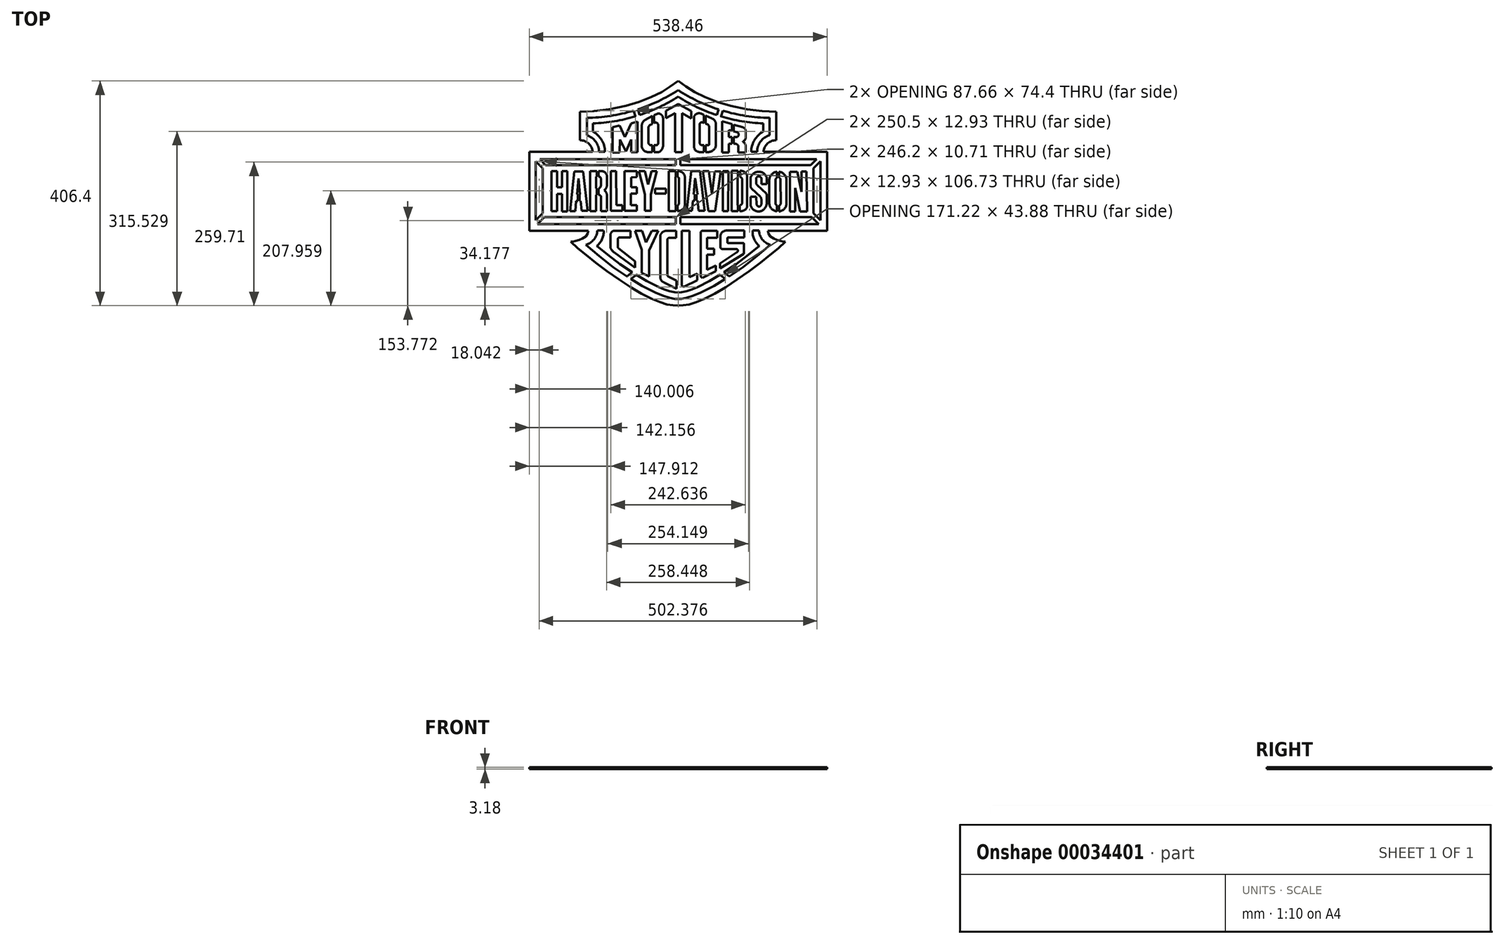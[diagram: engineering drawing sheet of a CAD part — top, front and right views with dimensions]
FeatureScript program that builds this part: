
annotation { "Feature Type Name" : "Feature", "Feature Type Description" : "" }
export const myFeature = defineFeature(function(context is Context, id is Id, definition is map)
    precondition{}
    {
        {
            var Q0;
            Q0=qCreatedBy(makeId("Top.planeOp"),FACE);
            var sketch = newSketch(context, id + "F0", { "sketchPlane" : qUnion([Q0])});
            skLineSegment(sketch, "E0", {"start": v(244.72, 45.2) * mm, "end": v(244.72, -35.68) * mm});
            skLineSegment(sketch, "E1", {"start": v(244.72, 45.2) * mm, "end": v(257.65, 58.13) * mm});
            skLineSegment(sketch, "E2", {"start": v(257.65, -48.6) * mm, "end": v(257.65, 58.13) * mm});
            skLineSegment(sketch, "E3", {"start": v(257.65, -48.6) * mm, "end": v(244.72, -35.68) * mm});
            skLineSegment(sketch, "E4", {"start": v(-134.72, -67.36) * mm, "end": v(-146, -67.36) * mm});
            skArc(sketch, "E5", {"start": v(-134.72, -67.36) * mm, "mid": v(-137.31, -82.59) * mm, "end": v(-146.79, -94.79) * mm});
            skLineSegment(sketch, "E6", {"start": v(-127.25, -111.1) * mm, "end": v(-146.79, -94.79) * mm});
            skLineSegment(sketch, "E7", {"start": v(-104.97, -127.73) * mm, "end": v(-127.25, -111.1) * mm});
            skLineSegment(sketch, "E8", {"start": v(-79.29, -145.04) * mm, "end": v(-104.97, -127.73) * mm});
            skLineSegment(sketch, "E9", {"start": v(-56.85, -158.5) * mm, "end": v(-79.29, -145.04) * mm});
            skLineSegment(sketch, "E10", {"start": v(-35.61, -169.16) * mm, "end": v(-56.85, -158.5) * mm});
            skLineSegment(sketch, "E11", {"start": v(-24.96, -173.53) * mm, "end": v(-35.61, -169.16) * mm});
            skLineSegment(sketch, "E12", {"start": v(-15.65, -176.7) * mm, "end": v(-24.96, -173.53) * mm});
            skLineSegment(sketch, "E13", {"start": v(-6.27, -178.92) * mm, "end": v(-15.65, -176.7) * mm});
            skLineSegment(sketch, "E14", {"start": v(0, -179.18) * mm, "end": v(-6.27, -178.92) * mm});
            skLineSegment(sketch, "E15", {"start": v(0, -179.18) * mm, "end": v(6.27, -178.92) * mm});
            skLineSegment(sketch, "E16", {"start": v(6.27, -178.92) * mm, "end": v(15.65, -176.7) * mm});
            skLineSegment(sketch, "E17", {"start": v(15.65, -176.7) * mm, "end": v(24.96, -173.53) * mm});
            skLineSegment(sketch, "E18", {"start": v(24.96, -173.53) * mm, "end": v(35.61, -169.16) * mm});
            skLineSegment(sketch, "E19", {"start": v(35.61, -169.16) * mm, "end": v(56.85, -158.5) * mm});
            skLineSegment(sketch, "E20", {"start": v(56.85, -158.5) * mm, "end": v(79.29, -145.04) * mm});
            skLineSegment(sketch, "E21", {"start": v(79.29, -145.04) * mm, "end": v(104.97, -127.73) * mm});
            skLineSegment(sketch, "E22", {"start": v(104.97, -127.73) * mm, "end": v(127.25, -111.1) * mm});
            skLineSegment(sketch, "E23", {"start": v(127.25, -111.1) * mm, "end": v(146.79, -94.79) * mm});
            skArc(sketch, "E24", {"start": v(134.72, -67.36) * mm, "mid": v(137.31, -82.59) * mm, "end": v(146.79, -94.79) * mm});
            skLineSegment(sketch, "E25", {"start": v(134.72, -67.36) * mm, "end": v(146, -67.36) * mm});
            skArc(sketch, "E26", {"start": v(146, -67.36) * mm, "mid": v(152.34, -83.41) * mm, "end": v(166.67, -93.03) * mm});
            skLineSegment(sketch, "E27", {"start": v(142.64, -113.33) * mm, "end": v(166.67, -93.03) * mm});
            skLineSegment(sketch, "E28", {"start": v(117.12, -133.46) * mm, "end": v(142.64, -113.33) * mm});
            skLineSegment(sketch, "E29", {"start": v(89.28, -152.75) * mm, "end": v(117.12, -133.46) * mm});
            skLineSegment(sketch, "E30", {"start": v(64.94, -167.27) * mm, "end": v(89.28, -152.75) * mm});
            skLineSegment(sketch, "E31", {"start": v(40.94, -179.2) * mm, "end": v(64.94, -167.27) * mm});
            skLineSegment(sketch, "E32", {"start": v(26.9, -184.96) * mm, "end": v(40.94, -179.2) * mm});
            skLineSegment(sketch, "E33", {"start": v(14.99, -188.9) * mm, "end": v(26.9, -184.96) * mm});
            skLineSegment(sketch, "E34", {"start": v(6.15, -190.75) * mm, "end": v(14.99, -188.9) * mm});
            skLineSegment(sketch, "E35", {"start": v(0, -190.96) * mm, "end": v(6.15, -190.75) * mm});
            skLineSegment(sketch, "E36", {"start": v(0, -190.96) * mm, "end": v(-6.15, -190.75) * mm});
            skLineSegment(sketch, "E37", {"start": v(-6.15, -190.75) * mm, "end": v(-14.99, -188.9) * mm});
            skLineSegment(sketch, "E38", {"start": v(-14.99, -188.9) * mm, "end": v(-26.9, -184.96) * mm});
            skLineSegment(sketch, "E39", {"start": v(-26.9, -184.96) * mm, "end": v(-40.94, -179.2) * mm});
            skLineSegment(sketch, "E40", {"start": v(-40.94, -179.2) * mm, "end": v(-64.94, -167.27) * mm});
            skLineSegment(sketch, "E41", {"start": v(-64.94, -167.27) * mm, "end": v(-89.28, -152.75) * mm});
            skLineSegment(sketch, "E42", {"start": v(-89.28, -152.75) * mm, "end": v(-117.12, -133.46) * mm});
            skLineSegment(sketch, "E43", {"start": v(-117.12, -133.46) * mm, "end": v(-142.64, -113.33) * mm});
            skLineSegment(sketch, "E44", {"start": v(-142.64, -113.33) * mm, "end": v(-166.67, -93.03) * mm});
            skArc(sketch, "E45", {"start": v(-146, -67.36) * mm, "mid": v(-152.34, -83.41) * mm, "end": v(-166.67, -93.03) * mm});
            skArc(sketch, "E46", {"start": v(0, 186.68) * mm, "mid": v(-79.05, 150) * mm, "end": v(-165.15, 136.55) * mm});
            skArc(sketch, "E47", {"start": v(0, 186.68) * mm, "mid": v(79.05, 150) * mm, "end": v(165.15, 136.55) * mm});
            skLineSegment(sketch, "E48", {"start": v(165.15, 104.94) * mm, "end": v(165.15, 136.55) * mm});
            skArc(sketch, "E49", {"start": v(165.15, 104.94) * mm, "mid": v(149.13, 93.71) * mm, "end": v(143.02, 75.13) * mm});
            skLineSegment(sketch, "E50", {"start": v(132.18, 75.13) * mm, "end": v(143.02, 75.13) * mm});
            skArc(sketch, "E51", {"start": v(153.86, 111.71) * mm, "mid": v(138.12, 96.32) * mm, "end": v(132.18, 75.13) * mm});
            skLineSegment(sketch, "E52", {"start": v(153.86, 111.71) * mm, "end": v(153.86, 126.62) * mm});
            skArc(sketch, "E53", {"start": v(0, 174.94) * mm, "mid": v(73.69, 140.46) * mm, "end": v(153.86, 126.62) * mm});
            skArc(sketch, "E54", {"start": v(0, 174.94) * mm, "mid": v(-73.69, 140.46) * mm, "end": v(-153.86, 126.62) * mm});
            skLineSegment(sketch, "E55", {"start": v(-153.86, 111.71) * mm, "end": v(-153.86, 126.62) * mm});
            skArc(sketch, "E56", {"start": v(-153.86, 111.71) * mm, "mid": v(-138.12, 96.32) * mm, "end": v(-132.18, 75.13) * mm});
            skLineSegment(sketch, "E57", {"start": v(-132.18, 75.13) * mm, "end": v(-143.02, 75.13) * mm});
            skArc(sketch, "E58", {"start": v(-165.15, 104.94) * mm, "mid": v(-149.13, 93.71) * mm, "end": v(-143.02, 75.13) * mm});
            skLineSegment(sketch, "E59", {"start": v(-165.15, 104.94) * mm, "end": v(-165.15, 136.55) * mm});
            skLineSegment(sketch, "E60", {"start": v(250.17, 61.87) * mm, "end": v(-250.17, 61.87) * mm});
            skLineSegment(sketch, "E61", {"start": v(239.46, 51.15) * mm, "end": v(250.17, 61.87) * mm});
            skLineSegment(sketch, "E62", {"start": v(239.46, 51.15) * mm, "end": v(-239.46, 51.15) * mm});
            skLineSegment(sketch, "E63", {"start": v(-239.46, 51.15) * mm, "end": v(-250.17, 61.87) * mm});
            skLineSegment(sketch, "E64", {"start": v(-244.72, 45.2) * mm, "end": v(-257.65, 58.13) * mm});
            skLineSegment(sketch, "E65", {"start": v(-244.72, 45.2) * mm, "end": v(-244.72, -35.68) * mm});
            skLineSegment(sketch, "E66", {"start": v(-257.65, -48.6) * mm, "end": v(-244.72, -35.68) * mm});
            skLineSegment(sketch, "E67", {"start": v(-257.65, -48.6) * mm, "end": v(-257.65, 58.13) * mm});
            skLineSegment(sketch, "E68", {"start": v(-163.33, -31.77) * mm, "end": v(-172.1, 39.88) * mm});
            skLineSegment(sketch, "E69", {"start": v(-174.33, -31.77) * mm, "end": v(-163.33, -31.77) * mm});
            skLineSegment(sketch, "E70", {"start": v(-176.14, -13.56) * mm, "end": v(-174.33, -31.77) * mm});
            skLineSegment(sketch, "E71", {"start": v(-178.4, -13.56) * mm, "end": v(-176.14, -13.56) * mm});
            skLineSegment(sketch, "E72", {"start": v(-178.4, -1.4) * mm, "end": v(-178.4, -13.56) * mm});
            skLineSegment(sketch, "E73", {"start": v(-178.4, -1.4) * mm, "end": v(-177.53, -1.4) * mm});
            skLineSegment(sketch, "E74", {"start": v(-177.53, -1.4) * mm, "end": v(-180.35, 27.13) * mm});
            skLineSegment(sketch, "E75", {"start": v(-180.35, 27.13) * mm, "end": v(-182.47, -1.4) * mm});
            skLineSegment(sketch, "E76", {"start": v(-182.47, -1.4) * mm, "end": v(-181.58, -1.4) * mm});
            skLineSegment(sketch, "E77", {"start": v(-181.58, -1.4) * mm, "end": v(-181.58, -13.56) * mm});
            skLineSegment(sketch, "E78", {"start": v(-184.18, -13.56) * mm, "end": v(-181.58, -13.56) * mm});
            skLineSegment(sketch, "E79", {"start": v(-186.06, -31.82) * mm, "end": v(-184.18, -13.56) * mm});
            skLineSegment(sketch, "E80", {"start": v(-195.2, -31.82) * mm, "end": v(-186.06, -31.82) * mm});
            skLineSegment(sketch, "E81", {"start": v(-187.4, 39.88) * mm, "end": v(-195.2, -31.82) * mm});
            skLineSegment(sketch, "E82", {"start": v(-172.1, 39.88) * mm, "end": v(-187.4, 39.88) * mm});
            skLineSegment(sketch, "E83", {"start": v(-219.07, 40.27) * mm, "end": v(-228.97, 40.27) * mm});
            skLineSegment(sketch, "E84", {"start": v(-219.07, 11.13) * mm, "end": v(-219.07, 40.27) * mm});
            skLineSegment(sketch, "E85", {"start": v(-210.2, 11.13) * mm, "end": v(-219.07, 11.13) * mm});
            skLineSegment(sketch, "E86", {"start": v(-210.2, 40.02) * mm, "end": v(-210.2, 11.13) * mm});
            skLineSegment(sketch, "E87", {"start": v(-200.08, 40.02) * mm, "end": v(-210.2, 40.02) * mm});
            skLineSegment(sketch, "E88", {"start": v(-200.08, -32.47) * mm, "end": v(-200.08, 40.02) * mm});
            skLineSegment(sketch, "E89", {"start": v(-209.7, -32.47) * mm, "end": v(-200.08, -32.47) * mm});
            skLineSegment(sketch, "E90", {"start": v(-209.7, -1.04) * mm, "end": v(-209.7, -32.47) * mm});
            skLineSegment(sketch, "E91", {"start": v(-219.09, -1.04) * mm, "end": v(-209.7, -1.04) * mm});
            skLineSegment(sketch, "E92", {"start": v(-219.09, -32.22) * mm, "end": v(-219.09, -1.04) * mm});
            skLineSegment(sketch, "E93", {"start": v(-228.97, -32.22) * mm, "end": v(-219.09, -32.22) * mm});
            skLineSegment(sketch, "E94", {"start": v(-228.97, 40.27) * mm, "end": v(-228.97, -32.22) * mm});
            skArc(sketch, "E95", {"start": v(-59.31, 132.93) * mm, "mid": v(-63.89, 128.57) * mm, "end": v(-65.63, 122.5) * mm});
            skLineSegment(sketch, "E96", {"start": v(-46.78, 139.7) * mm, "end": v(-59.31, 132.93) * mm});
            skLineSegment(sketch, "E97", {"start": v(-46.78, 125.67) * mm, "end": v(-46.78, 139.7) * mm});
            skLineSegment(sketch, "E98", {"start": v(-50.02, 124.14) * mm, "end": v(-46.78, 125.67) * mm});
            skArc(sketch, "E99", {"start": v(-50.02, 124.14) * mm, "mid": v(-52.73, 121.7) * mm, "end": v(-53.61, 118.16) * mm});
            skLineSegment(sketch, "E100", {"start": v(-53.61, 91.84) * mm, "end": v(-53.61, 118.16) * mm});
            skArc(sketch, "E101", {"start": v(-53.61, 91.84) * mm, "mid": v(-52.12, 88.37) * mm, "end": v(-48.59, 87.06) * mm});
            skLineSegment(sketch, "E102", {"start": v(-46.78, 87.06) * mm, "end": v(-48.59, 87.06) * mm});
            skLineSegment(sketch, "E103", {"start": v(-46.78, 74.46) * mm, "end": v(-46.78, 87.06) * mm});
            skLineSegment(sketch, "E104", {"start": v(-46.78, 74.46) * mm, "end": v(-53.69, 74.46) * mm});
            skArc(sketch, "E105", {"start": v(-65.63, 84.09) * mm, "mid": v(-61.35, 77.17) * mm, "end": v(-53.69, 74.46) * mm});
            skLineSegment(sketch, "E106", {"start": v(-65.63, 122.5) * mm, "end": v(-65.63, 84.09) * mm});
            skLineSegment(sketch, "E107", {"start": v(23.7, 148.6) * mm, "end": v(0.36, 161.32) * mm});
            skLineSegment(sketch, "E108", {"start": v(23.7, 135.49) * mm, "end": v(23.7, 148.6) * mm});
            skLineSegment(sketch, "E109", {"start": v(7.5, 145.04) * mm, "end": v(23.7, 135.49) * mm});
            skLineSegment(sketch, "E110", {"start": v(7.5, 74.74) * mm, "end": v(7.5, 145.04) * mm});
            skLineSegment(sketch, "E111", {"start": v(-5.74, 74.74) * mm, "end": v(7.5, 74.74) * mm});
            skLineSegment(sketch, "E112", {"start": v(-5.74, 145.04) * mm, "end": v(-5.74, 74.74) * mm});
            skLineSegment(sketch, "E113", {"start": v(-22.1, 136.3) * mm, "end": v(-5.74, 145.04) * mm});
            skLineSegment(sketch, "E114", {"start": v(-22.1, 149.33) * mm, "end": v(-22.1, 136.3) * mm});
            skLineSegment(sketch, "E115", {"start": v(0.36, 161.32) * mm, "end": v(-22.1, 149.33) * mm});
            skArc(sketch, "E116", {"start": v(44.13, -67.65) * mm, "mid": v(41.88, -68.58) * mm, "end": v(40.95, -70.83) * mm});
            skLineSegment(sketch, "E117", {"start": v(44.13, -67.65) * mm, "end": v(70.7, -67.65) * mm});
            skLineSegment(sketch, "E118", {"start": v(70.7, -67.65) * mm, "end": v(70.7, -80.36) * mm});
            skLineSegment(sketch, "E119", {"start": v(70.7, -80.36) * mm, "end": v(52.22, -80.36) * mm});
            skLineSegment(sketch, "E120", {"start": v(52.22, -80.36) * mm, "end": v(52.22, -100.28) * mm});
            skLineSegment(sketch, "E121", {"start": v(52.22, -100.28) * mm, "end": v(65.28, -100.28) * mm});
            skLineSegment(sketch, "E122", {"start": v(65.28, -100.28) * mm, "end": v(65.28, -111.05) * mm});
            skLineSegment(sketch, "E123", {"start": v(65.28, -111.05) * mm, "end": v(52.38, -111.05) * mm});
            skLineSegment(sketch, "E124", {"start": v(52.38, -111.05) * mm, "end": v(52.38, -137.9) * mm});
            skLineSegment(sketch, "E125", {"start": v(52.38, -137.9) * mm, "end": v(67.97, -130.3) * mm});
            skLineSegment(sketch, "E126", {"start": v(67.97, -130.3) * mm, "end": v(67.97, -140.67) * mm});
            skLineSegment(sketch, "E127", {"start": v(67.97, -140.67) * mm, "end": v(45.58, -152.16) * mm});
            skArc(sketch, "E128", {"start": v(40.95, -149.33) * mm, "mid": v(42.47, -152.04) * mm, "end": v(45.58, -152.16) * mm});
            skLineSegment(sketch, "E129", {"start": v(40.95, -70.83) * mm, "end": v(40.95, -149.33) * mm});
            skArc(sketch, "E130", {"start": v(-21.33, -67.84) * mm, "mid": v(-29.3, -71.25) * mm, "end": v(-32.32, -79.37) * mm});
            skLineSegment(sketch, "E131", {"start": v(-3.53, -67.84) * mm, "end": v(-21.33, -67.84) * mm});
            skLineSegment(sketch, "E132", {"start": v(-3.53, -67.84) * mm, "end": v(-3.53, -80.21) * mm});
            skLineSegment(sketch, "E133", {"start": v(-3.53, -80.21) * mm, "end": v(-15.23, -80.21) * mm});
            skArc(sketch, "E134", {"start": v(-15.23, -80.21) * mm, "mid": v(-18.15, -81.35) * mm, "end": v(-19.51, -84.17) * mm});
            skLineSegment(sketch, "E135", {"start": v(-19.51, -84.17) * mm, "end": v(-19.51, -145.33) * mm});
            skArc(sketch, "E136", {"start": v(-19.51, -145.33) * mm, "mid": v(-19.23, -148.69) * mm, "end": v(-16.83, -151.07) * mm});
            skLineSegment(sketch, "E137", {"start": v(-2.61, -157.57) * mm, "end": v(-16.83, -151.07) * mm});
            skLineSegment(sketch, "E138", {"start": v(-2.61, -157.57) * mm, "end": v(-2.61, -172.19) * mm});
            skLineSegment(sketch, "E139", {"start": v(-2.61, -172.19) * mm, "end": v(-25.56, -161.35) * mm});
            skArc(sketch, "E140", {"start": v(-32.32, -150.77) * mm, "mid": v(-30.47, -157.03) * mm, "end": v(-25.56, -161.35) * mm});
            skLineSegment(sketch, "E141", {"start": v(-32.32, -79.37) * mm, "end": v(-32.32, -150.77) * mm});
            skLineSegment(sketch, "E142", {"start": v(108.48, 40.64) * mm, "end": v(97, 40.64) * mm});
            skLineSegment(sketch, "E143", {"start": v(108.48, 40.64) * mm, "end": v(108.48, 29.42) * mm});
            skLineSegment(sketch, "E144", {"start": v(108.48, 29.42) * mm, "end": v(107.34, 29.42) * mm});
            skLineSegment(sketch, "E145", {"start": v(107.34, 29.42) * mm, "end": v(107.34, -21.54) * mm});
            skLineSegment(sketch, "E146", {"start": v(107.34, -21.54) * mm, "end": v(108.48, -21.54) * mm});
            skLineSegment(sketch, "E147", {"start": v(108.48, -21.54) * mm, "end": v(108.48, -31.97) * mm});
            skLineSegment(sketch, "E148", {"start": v(97, -31.97) * mm, "end": v(108.48, -31.97) * mm});
            skLineSegment(sketch, "E149", {"start": v(97, 40.64) * mm, "end": v(97, -31.97) * mm});
            skArc(sketch, "E150", {"start": v(125.02, 29.68) * mm, "mid": v(121.8, 37.43) * mm, "end": v(114.07, 40.64) * mm});
            skLineSegment(sketch, "E151", {"start": v(125.02, 29.68) * mm, "end": v(125.02, -21.43) * mm});
            skArc(sketch, "E152", {"start": v(114.48, -31.97) * mm, "mid": v(121.93, -28.88) * mm, "end": v(125.02, -21.43) * mm});
            skLineSegment(sketch, "E153", {"start": v(111.65, -31.97) * mm, "end": v(114.48, -31.97) * mm});
            skLineSegment(sketch, "E154", {"start": v(111.65, -31.97) * mm, "end": v(111.65, -21.54) * mm});
            skLineSegment(sketch, "E155", {"start": v(111.65, -21.54) * mm, "end": v(111.7, -21.54) * mm});
            skArc(sketch, "E156", {"start": v(111.7, -21.54) * mm, "mid": v(114.53, -20.36) * mm, "end": v(115.7, -17.53) * mm});
            skLineSegment(sketch, "E157", {"start": v(115.7, 25.44) * mm, "end": v(115.7, -17.53) * mm});
            skArc(sketch, "E158", {"start": v(115.7, 25.44) * mm, "mid": v(114.54, 28.25) * mm, "end": v(111.72, 29.42) * mm});
            skLineSegment(sketch, "E159", {"start": v(111.72, 29.42) * mm, "end": v(111.72, 40.64) * mm});
            skLineSegment(sketch, "E160", {"start": v(114.07, 40.64) * mm, "end": v(111.72, 40.64) * mm});
            skLineSegment(sketch, "E161", {"start": v(90.69, -31.98) * mm, "end": v(90.96, 39.99) * mm});
            skLineSegment(sketch, "E162", {"start": v(81.02, -31.98) * mm, "end": v(90.69, -31.98) * mm});
            skLineSegment(sketch, "E163", {"start": v(81.02, 39.99) * mm, "end": v(81.02, -31.98) * mm});
            skLineSegment(sketch, "E164", {"start": v(90.96, 39.99) * mm, "end": v(81.02, 39.99) * mm});
            skArc(sketch, "E165", {"start": v(178.9, 39.2) * mm, "mid": v(168.96, 34.19) * mm, "end": v(164.96, 23.8) * mm});
            skLineSegment(sketch, "E166", {"start": v(178.9, 39.2) * mm, "end": v(178.9, 28.43) * mm});
            skArc(sketch, "E167", {"start": v(178.9, 28.43) * mm, "mid": v(177.1, 26.82) * mm, "end": v(176.28, 24.54) * mm});
            skLineSegment(sketch, "E168", {"start": v(176.28, -18.95) * mm, "end": v(176.28, 24.54) * mm});
            skArc(sketch, "E169", {"start": v(176.28, -18.95) * mm, "mid": v(177.26, -20.79) * mm, "end": v(178.9, -22.05) * mm});
            skLineSegment(sketch, "E170", {"start": v(178.9, -22.05) * mm, "end": v(178.9, -32.66) * mm});
            skArc(sketch, "E171", {"start": v(164.96, -17.56) * mm, "mid": v(168.98, -27.84) * mm, "end": v(178.9, -32.66) * mm});
            skLineSegment(sketch, "E172", {"start": v(164.96, 23.8) * mm, "end": v(164.96, -17.56) * mm});
            skLineSegment(sketch, "E173", {"start": v(47.6, -31.35) * mm, "end": v(39.5, 40.48) * mm});
            skLineSegment(sketch, "E174", {"start": v(36.95, -31.35) * mm, "end": v(47.6, -31.35) * mm});
            skLineSegment(sketch, "E175", {"start": v(35.29, -13.26) * mm, "end": v(36.95, -31.35) * mm});
            skLineSegment(sketch, "E176", {"start": v(33.08, -13.26) * mm, "end": v(35.29, -13.26) * mm});
            skLineSegment(sketch, "E177", {"start": v(33.08, -1.43) * mm, "end": v(33.08, -13.26) * mm});
            skLineSegment(sketch, "E178", {"start": v(33.08, -1.43) * mm, "end": v(34.92, -1.43) * mm});
            skLineSegment(sketch, "E179", {"start": v(34.92, -1.43) * mm, "end": v(30.92, 27.63) * mm});
            skLineSegment(sketch, "E180", {"start": v(30.92, 27.63) * mm, "end": v(28.2, -1.43) * mm});
            skLineSegment(sketch, "E181", {"start": v(28.2, -1.43) * mm, "end": v(29.9, -1.43) * mm});
            skLineSegment(sketch, "E182", {"start": v(29.9, -1.43) * mm, "end": v(29.9, -13.26) * mm});
            skLineSegment(sketch, "E183", {"start": v(26.68, -13.26) * mm, "end": v(29.9, -13.26) * mm});
            skLineSegment(sketch, "E184", {"start": v(25.22, -31.78) * mm, "end": v(26.68, -13.26) * mm});
            skLineSegment(sketch, "E185", {"start": v(15.63, -31.78) * mm, "end": v(25.22, -31.78) * mm});
            skLineSegment(sketch, "E186", {"start": v(23.95, 40.48) * mm, "end": v(15.63, -31.78) * mm});
            skLineSegment(sketch, "E187", {"start": v(39.5, 40.48) * mm, "end": v(23.95, 40.48) * mm});
            skLineSegment(sketch, "E188", {"start": v(61.12, -1.32) * mm, "end": v(55.39, 40.26) * mm});
            skLineSegment(sketch, "E189", {"start": v(66.5, 39.9) * mm, "end": v(61.12, -1.32) * mm});
            skLineSegment(sketch, "E190", {"start": v(77.26, 39.9) * mm, "end": v(66.5, 39.9) * mm});
            skLineSegment(sketch, "E191", {"start": v(67.22, -32.15) * mm, "end": v(77.26, 39.9) * mm});
            skLineSegment(sketch, "E192", {"start": v(54.67, -32.15) * mm, "end": v(67.22, -32.15) * mm});
            skLineSegment(sketch, "E193", {"start": v(45, 40.26) * mm, "end": v(54.67, -32.15) * mm});
            skLineSegment(sketch, "E194", {"start": v(55.39, 40.26) * mm, "end": v(45, 40.26) * mm});
            skLineSegment(sketch, "E195", {"start": v(-54.1, 16.38) * mm, "end": v(-59.83, 40.4) * mm});
            skLineSegment(sketch, "E196", {"start": v(-48, 40.04) * mm, "end": v(-54.1, 16.38) * mm});
            skLineSegment(sketch, "E197", {"start": v(-38.32, 40.04) * mm, "end": v(-48, 40.04) * mm});
            skLineSegment(sketch, "E198", {"start": v(-49.43, -1.54) * mm, "end": v(-38.32, 40.04) * mm});
            skLineSegment(sketch, "E199", {"start": v(-49.07, -31.3) * mm, "end": v(-49.43, -1.54) * mm});
            skLineSegment(sketch, "E200", {"start": v(-60.2, -31.3) * mm, "end": v(-49.07, -31.3) * mm});
            skLineSegment(sketch, "E201", {"start": v(-59.83, -1.54) * mm, "end": v(-60.2, -31.3) * mm});
            skLineSegment(sketch, "E202", {"start": v(-70.59, 40.4) * mm, "end": v(-59.83, -1.54) * mm});
            skLineSegment(sketch, "E203", {"start": v(-59.83, 40.4) * mm, "end": v(-70.59, 40.4) * mm});
            skLineSegment(sketch, "E204", {"start": v(-21.86, -0.34) * mm, "end": v(-21.86, 8.72) * mm});
            skLineSegment(sketch, "E205", {"start": v(-41.52, -0.34) * mm, "end": v(-21.86, -0.34) * mm});
            skLineSegment(sketch, "E206", {"start": v(-41.52, 8.72) * mm, "end": v(-41.52, -0.34) * mm});
            skLineSegment(sketch, "E207", {"start": v(-21.86, 8.72) * mm, "end": v(-41.52, 8.72) * mm});
            skLineSegment(sketch, "E208", {"start": v(-74.62, 29.42) * mm, "end": v(-74.62, 40.27) * mm});
            skLineSegment(sketch, "E209", {"start": v(-85, 28.97) * mm, "end": v(-74.62, 29.42) * mm});
            skLineSegment(sketch, "E210", {"start": v(-85, 11.13) * mm, "end": v(-85, 28.97) * mm});
            skLineSegment(sketch, "E211", {"start": v(-74.84, 11.13) * mm, "end": v(-85, 11.13) * mm});
            skLineSegment(sketch, "E212", {"start": v(-74.84, -0.17) * mm, "end": v(-74.84, 11.13) * mm});
            skLineSegment(sketch, "E213", {"start": v(-85.23, -0.17) * mm, "end": v(-74.84, -0.17) * mm});
            skLineSegment(sketch, "E214", {"start": v(-85.23, -21.63) * mm, "end": v(-85.23, -0.17) * mm});
            skLineSegment(sketch, "E215", {"start": v(-74.83, -21.63) * mm, "end": v(-85.23, -21.63) * mm});
            skLineSegment(sketch, "E216", {"start": v(-74.83, -31.32) * mm, "end": v(-74.83, -21.63) * mm});
            skLineSegment(sketch, "E217", {"start": v(-96.97, -31.32) * mm, "end": v(-74.83, -31.32) * mm});
            skLineSegment(sketch, "E218", {"start": v(-96.97, 40.27) * mm, "end": v(-96.97, -31.32) * mm});
            skLineSegment(sketch, "E219", {"start": v(-74.62, 40.27) * mm, "end": v(-96.97, 40.27) * mm});
            skLineSegment(sketch, "E220", {"start": v(-111.8, -21.12) * mm, "end": v(-111.85, 40.36) * mm});
            skLineSegment(sketch, "E221", {"start": v(-100.61, -21.12) * mm, "end": v(-111.8, -21.12) * mm});
            skLineSegment(sketch, "E222", {"start": v(-100.61, -31.26) * mm, "end": v(-100.61, -21.12) * mm});
            skLineSegment(sketch, "E223", {"start": v(-121.87, -31.26) * mm, "end": v(-100.61, -31.26) * mm});
            skLineSegment(sketch, "E224", {"start": v(-121.87, 40.36) * mm, "end": v(-121.87, -31.26) * mm});
            skLineSegment(sketch, "E225", {"start": v(-111.85, 40.36) * mm, "end": v(-121.87, 40.36) * mm});
            skLineSegment(sketch, "E226", {"start": v(-65.61, -101.82) * mm, "end": v(-65.61, -143.7) * mm});
            skLineSegment(sketch, "E227", {"start": v(-78.06, -67.63) * mm, "end": v(-65.61, -101.82) * mm});
            skLineSegment(sketch, "E228", {"start": v(-65.38, -67.63) * mm, "end": v(-78.06, -67.63) * mm});
            skLineSegment(sketch, "E229", {"start": v(-58.37, -88.46) * mm, "end": v(-65.38, -67.63) * mm});
            skLineSegment(sketch, "E230", {"start": v(-47.05, -67.86) * mm, "end": v(-58.37, -88.46) * mm});
            skLineSegment(sketch, "E231", {"start": v(-36.18, -67.86) * mm, "end": v(-47.05, -67.86) * mm});
            skLineSegment(sketch, "E232", {"start": v(-52.7, -103.4) * mm, "end": v(-36.18, -67.86) * mm});
            skLineSegment(sketch, "E233", {"start": v(-52.7, -150.5) * mm, "end": v(-52.7, -103.4) * mm});
            skLineSegment(sketch, "E234", {"start": v(-65.61, -143.7) * mm, "end": v(-52.7, -150.5) * mm});
            skLineSegment(sketch, "E235", {"start": v(222.96, 3.08) * mm, "end": v(222.96, 39.35) * mm});
            skLineSegment(sketch, "E236", {"start": v(222.96, 39.35) * mm, "end": v(232.35, 39.35) * mm});
            skLineSegment(sketch, "E237", {"start": v(232.35, 39.35) * mm, "end": v(233.25, -32.66) * mm});
            skLineSegment(sketch, "E238", {"start": v(233.25, -32.66) * mm, "end": v(220.8, -32.66) * mm});
            skLineSegment(sketch, "E239", {"start": v(220.8, -32.66) * mm, "end": v(211.49, 9.78) * mm});
            skLineSegment(sketch, "E240", {"start": v(211.49, 9.78) * mm, "end": v(211.49, -32.66) * mm});
            skLineSegment(sketch, "E241", {"start": v(211.49, -32.66) * mm, "end": v(202.14, -32.66) * mm});
            skLineSegment(sketch, "E242", {"start": v(202.14, -32.66) * mm, "end": v(202.14, 39.2) * mm});
            skLineSegment(sketch, "E243", {"start": v(202.14, 39.2) * mm, "end": v(215.53, 39.2) * mm});
            skLineSegment(sketch, "E244", {"start": v(215.53, 39.2) * mm, "end": v(222.96, 3.08) * mm});
            skArc(sketch, "E245", {"start": v(-116.67, -67.53) * mm, "mid": v(-120.83, -71.06) * mm, "end": v(-122.38, -76.3) * mm});
            skLineSegment(sketch, "E246", {"start": v(-116.67, -67.53) * mm, "end": v(-86.2, -67.53) * mm});
            skLineSegment(sketch, "E247", {"start": v(-86.2, -67.53) * mm, "end": v(-86.2, -79.55) * mm});
            skLineSegment(sketch, "E248", {"start": v(-86.2, -79.55) * mm, "end": v(-105.7, -79.55) * mm});
            skArc(sketch, "E249", {"start": v(-105.7, -79.55) * mm, "mid": v(-107.94, -80.48) * mm, "end": v(-108.87, -82.72) * mm});
            skLineSegment(sketch, "E250", {"start": v(-108.87, -82.72) * mm, "end": v(-108.87, -96.85) * mm});
            skArc(sketch, "E251", {"start": v(-108.87, -96.85) * mm, "mid": v(-108.55, -98.23) * mm, "end": v(-107.68, -99.33) * mm});
            skLineSegment(sketch, "E252", {"start": v(-107.68, -99.33) * mm, "end": v(-78.06, -123.1) * mm});
            skLineSegment(sketch, "E253", {"start": v(-78.06, -123.1) * mm, "end": v(-78.06, -134.64) * mm});
            skLineSegment(sketch, "E254", {"start": v(-78.06, -134.64) * mm, "end": v(-115.9, -106.56) * mm});
            skArc(sketch, "E255", {"start": v(-122.38, -98.18) * mm, "mid": v(-119.72, -102.82) * mm, "end": v(-115.9, -106.56) * mm});
            skLineSegment(sketch, "E256", {"start": v(-122.38, -98.18) * mm, "end": v(-122.38, -76.3) * mm});
            skArc(sketch, "E257", {"start": v(87.2, -67.22) * mm, "mid": v(79.66, -70.35) * mm, "end": v(76.54, -77.89) * mm});
            skLineSegment(sketch, "E258", {"start": v(87.2, -67.22) * mm, "end": v(119.45, -67.22) * mm});
            skLineSegment(sketch, "E259", {"start": v(119.45, -67.22) * mm, "end": v(119.45, -79.7) * mm});
            skLineSegment(sketch, "E260", {"start": v(119.45, -79.7) * mm, "end": v(90.62, -79.7) * mm});
            skArc(sketch, "E261", {"start": v(90.62, -79.7) * mm, "mid": v(89.5, -80.17) * mm, "end": v(89.03, -81.3) * mm});
            skLineSegment(sketch, "E262", {"start": v(89.03, -81.3) * mm, "end": v(89.03, -88.2) * mm});
            skArc(sketch, "E263", {"start": v(89.03, -88.2) * mm, "mid": v(89.5, -89.33) * mm, "end": v(90.62, -89.8) * mm});
            skLineSegment(sketch, "E264", {"start": v(90.62, -89.8) * mm, "end": v(117.34, -89.8) * mm});
            skArc(sketch, "E265", {"start": v(118.92, -91.38) * mm, "mid": v(118.46, -90.26) * mm, "end": v(117.34, -89.8) * mm});
            skLineSegment(sketch, "E266", {"start": v(118.92, -91.38) * mm, "end": v(118.92, -108.33) * mm});
            skArc(sketch, "E267", {"start": v(118.17, -109.68) * mm, "mid": v(118.72, -109.1) * mm, "end": v(118.92, -108.33) * mm});
            skLineSegment(sketch, "E268", {"start": v(118.17, -109.68) * mm, "end": v(76.09, -135.87) * mm});
            skLineSegment(sketch, "E269", {"start": v(76.09, -135.87) * mm, "end": v(76.09, -126.54) * mm});
            skLineSegment(sketch, "E270", {"start": v(76.09, -126.54) * mm, "end": v(106.61, -106.3) * mm});
            skArc(sketch, "E271", {"start": v(106.61, -106.3) * mm, "mid": v(107.9, -102.74) * mm, "end": v(104.86, -100.48) * mm});
            skLineSegment(sketch, "E272", {"start": v(104.86, -100.48) * mm, "end": v(79.71, -100.48) * mm});
            skArc(sketch, "E273", {"start": v(76.54, -97.3) * mm, "mid": v(77.47, -99.55) * mm, "end": v(79.71, -100.48) * mm});
            skLineSegment(sketch, "E274", {"start": v(76.54, -97.3) * mm, "end": v(76.54, -77.89) * mm});
            skLineSegment(sketch, "E275", {"start": v(-94.47, 75.87) * mm, "end": v(-105.13, 97.18) * mm});
            skLineSegment(sketch, "E276", {"start": v(-105.13, 97.18) * mm, "end": v(-105.77, 74.16) * mm});
            skLineSegment(sketch, "E277", {"start": v(-105.77, 74.16) * mm, "end": v(-118.34, 74.16) * mm});
            skLineSegment(sketch, "E278", {"start": v(-118.34, 74.16) * mm, "end": v(-118.34, 119.78) * mm});
            skLineSegment(sketch, "E279", {"start": v(-118.34, 119.78) * mm, "end": v(-105.55, 122.55) * mm});
            skLineSegment(sketch, "E280", {"start": v(-105.55, 122.55) * mm, "end": v(-96.39, 102.08) * mm});
            skLineSegment(sketch, "E281", {"start": v(-96.39, 102.08) * mm, "end": v(-84.88, 126.6) * mm});
            skLineSegment(sketch, "E282", {"start": v(-84.88, 126.6) * mm, "end": v(-73.15, 129.8) * mm});
            skLineSegment(sketch, "E283", {"start": v(-73.15, 129.8) * mm, "end": v(-73.15, 74.8) * mm});
            skLineSegment(sketch, "E284", {"start": v(-73.15, 74.8) * mm, "end": v(-84.66, 74.8) * mm});
            skLineSegment(sketch, "E285", {"start": v(-84.66, 74.8) * mm, "end": v(-84.66, 97.6) * mm});
            skLineSegment(sketch, "E286", {"start": v(-84.66, 97.6) * mm, "end": v(-94.47, 75.87) * mm});
            skLineSegment(sketch, "E287", {"start": v(109.27, 105.45) * mm, "end": v(109.27, 107.2) * mm});
            skArc(sketch, "E288", {"start": v(109.27, 107.2) * mm, "mid": v(108.47, 109.53) * mm, "end": v(106.4, 110.87) * mm});
            skLineSegment(sketch, "E289", {"start": v(106.4, 110.87) * mm, "end": v(100.75, 112.26) * mm});
            skLineSegment(sketch, "E290", {"start": v(100.75, 124.38) * mm, "end": v(100.75, 112.26) * mm});
            skLineSegment(sketch, "E291", {"start": v(100.75, 124.38) * mm, "end": v(117.01, 119.62) * mm});
            skArc(sketch, "E292", {"start": v(122.24, 112.65) * mm, "mid": v(120.79, 117) * mm, "end": v(117.01, 119.62) * mm});
            skLineSegment(sketch, "E293", {"start": v(122.24, 112.65) * mm, "end": v(122.24, 101) * mm});
            skArc(sketch, "E294", {"start": v(116.82, 93.75) * mm, "mid": v(120.73, 96.48) * mm, "end": v(122.24, 101) * mm});
            skArc(sketch, "E295", {"start": v(122.24, 84.87) * mm, "mid": v(120.78, 90.07) * mm, "end": v(116.82, 93.75) * mm});
            skLineSegment(sketch, "E296", {"start": v(122.24, 74.23) * mm, "end": v(122.24, 84.87) * mm});
            skLineSegment(sketch, "E297", {"start": v(108.99, 74.23) * mm, "end": v(122.24, 74.23) * mm});
            skLineSegment(sketch, "E298", {"start": v(108.99, 84.2) * mm, "end": v(108.99, 74.23) * mm});
            skArc(sketch, "E299", {"start": v(108.99, 84.2) * mm, "mid": v(107.4, 88.04) * mm, "end": v(103.55, 89.64) * mm});
            skLineSegment(sketch, "E300", {"start": v(100.75, 89.64) * mm, "end": v(103.55, 89.64) * mm});
            skLineSegment(sketch, "E301", {"start": v(100.75, 101.93) * mm, "end": v(100.75, 89.64) * mm});
            skLineSegment(sketch, "E302", {"start": v(100.75, 101.93) * mm, "end": v(105.63, 101.93) * mm});
            skArc(sketch, "E303", {"start": v(105.63, 101.93) * mm, "mid": v(108.16, 102.95) * mm, "end": v(109.27, 105.45) * mm});
            skLineSegment(sketch, "E304", {"start": v(-139.71, 26.65) * mm, "end": v(-139.71, 14.1) * mm});
            skArc(sketch, "E305", {"start": v(-139.71, 26.65) * mm, "mid": v(-140.78, 29.22) * mm, "end": v(-143.35, 30.28) * mm});
            skLineSegment(sketch, "E306", {"start": v(-143.35, 30.28) * mm, "end": v(-143.71, 30.28) * mm});
            skLineSegment(sketch, "E307", {"start": v(-143.71, 30.28) * mm, "end": v(-143.71, 40.35) * mm});
            skLineSegment(sketch, "E308", {"start": v(-143.71, 40.35) * mm, "end": v(-138.63, 40.35) * mm});
            skArc(sketch, "E309", {"start": v(-128.57, 30.3) * mm, "mid": v(-131.52, 37.4) * mm, "end": v(-138.63, 40.35) * mm});
            skLineSegment(sketch, "E310", {"start": v(-128.57, 30.3) * mm, "end": v(-128.57, 15.62) * mm});
            skArc(sketch, "E311", {"start": v(-133.56, 5.58) * mm, "mid": v(-129.89, 10.02) * mm, "end": v(-128.57, 15.62) * mm});
            skArc(sketch, "E312", {"start": v(-128.9, -1.64) * mm, "mid": v(-130.54, 2.41) * mm, "end": v(-133.56, 5.58) * mm});
            skLineSegment(sketch, "E313", {"start": v(-128.9, -31.97) * mm, "end": v(-128.9, -1.64) * mm});
            skLineSegment(sketch, "E314", {"start": v(-139.18, -31.97) * mm, "end": v(-128.9, -31.97) * mm});
            skLineSegment(sketch, "E315", {"start": v(-139.18, -7.03) * mm, "end": v(-139.18, -31.97) * mm});
            skArc(sketch, "E316", {"start": v(-139.18, -7.03) * mm, "mid": v(-140.44, -3.99) * mm, "end": v(-143.48, -2.73) * mm});
            skLineSegment(sketch, "E317", {"start": v(-143.71, -2.73) * mm, "end": v(-143.48, -2.73) * mm});
            skLineSegment(sketch, "E318", {"start": v(-143.71, -2.73) * mm, "end": v(-143.71, 9.04) * mm});
            skLineSegment(sketch, "E319", {"start": v(-143.71, 9.04) * mm, "end": v(-143.24, 9.04) * mm});
            skArc(sketch, "E320", {"start": v(-143.24, 9.04) * mm, "mid": v(-140.68, 11.02) * mm, "end": v(-139.71, 14.1) * mm});
            skLineSegment(sketch, "E321", {"start": v(254.47, -55.9) * mm, "end": v(241.54, -42.96) * mm});
            skLineSegment(sketch, "E322", {"start": v(254.47, -55.9) * mm, "end": v(-254.47, -55.9) * mm});
            skLineSegment(sketch, "E323", {"start": v(-254.47, -55.9) * mm, "end": v(-241.54, -42.96) * mm});
            skLineSegment(sketch, "E324", {"start": v(241.54, -42.96) * mm, "end": v(-241.54, -42.96) * mm});
            skLineSegment(sketch, "E325", {"start": v(-159.39, 40.35) * mm, "end": v(-159.39, -32.18) * mm});
            skLineSegment(sketch, "E326", {"start": v(-159.39, 40.35) * mm, "end": v(-146.89, 40.35) * mm});
            skLineSegment(sketch, "E327", {"start": v(-146.89, 40.35) * mm, "end": v(-146.89, 30.28) * mm});
            skLineSegment(sketch, "E328", {"start": v(-146.89, 30.28) * mm, "end": v(-148.09, 30.28) * mm});
            skLineSegment(sketch, "E329", {"start": v(-148.09, 30.28) * mm, "end": v(-148.09, 9.04) * mm});
            skLineSegment(sketch, "E330", {"start": v(-148.09, 9.04) * mm, "end": v(-146.89, 9.04) * mm});
            skLineSegment(sketch, "E331", {"start": v(-146.89, 9.04) * mm, "end": v(-146.89, -2.73) * mm});
            skLineSegment(sketch, "E332", {"start": v(-148.03, -2.73) * mm, "end": v(-146.89, -2.73) * mm});
            skLineSegment(sketch, "E333", {"start": v(-148.03, -32.18) * mm, "end": v(-148.03, -2.73) * mm});
            skLineSegment(sketch, "E334", {"start": v(-159.39, -32.18) * mm, "end": v(-148.03, -32.18) * mm});
            skLineSegment(sketch, "E335", {"start": v(79.55, 130.58) * mm, "end": v(79.55, 74.13) * mm});
            skLineSegment(sketch, "E336", {"start": v(79.55, 130.58) * mm, "end": v(97.57, 125.3) * mm});
            skLineSegment(sketch, "E337", {"start": v(97.57, 125.3) * mm, "end": v(97.57, 113.04) * mm});
            skLineSegment(sketch, "E338", {"start": v(97.57, 113.04) * mm, "end": v(91.95, 114.42) * mm});
            skLineSegment(sketch, "E339", {"start": v(91.95, 114.42) * mm, "end": v(91.95, 101.93) * mm});
            skLineSegment(sketch, "E340", {"start": v(91.95, 101.93) * mm, "end": v(97.57, 101.93) * mm});
            skLineSegment(sketch, "E341", {"start": v(97.57, 101.93) * mm, "end": v(97.57, 89.64) * mm});
            skLineSegment(sketch, "E342", {"start": v(91.6, 89.64) * mm, "end": v(97.57, 89.64) * mm});
            skLineSegment(sketch, "E343", {"start": v(91.6, 74.13) * mm, "end": v(91.6, 89.64) * mm});
            skLineSegment(sketch, "E344", {"start": v(79.55, 74.13) * mm, "end": v(91.6, 74.13) * mm});
            skLineSegment(sketch, "E345", {"start": v(56.26, 119.56) * mm, "end": v(56.26, 88.99) * mm});
            skArc(sketch, "E346", {"start": v(56.26, 119.56) * mm, "mid": v(55.51, 122.5) * mm, "end": v(53.46, 124.73) * mm});
            skLineSegment(sketch, "E347", {"start": v(50.06, 126.02) * mm, "end": v(53.46, 124.73) * mm});
            skLineSegment(sketch, "E348", {"start": v(50.06, 126.02) * mm, "end": v(50.06, 140.44) * mm});
            skLineSegment(sketch, "E349", {"start": v(50.06, 140.44) * mm, "end": v(61.12, 135.69) * mm});
            skArc(sketch, "E350", {"start": v(68.55, 124.42) * mm, "mid": v(66.52, 131.16) * mm, "end": v(61.12, 135.69) * mm});
            skLineSegment(sketch, "E351", {"start": v(68.55, 124.42) * mm, "end": v(68.55, 86.37) * mm});
            skArc(sketch, "E352", {"start": v(54.16, 74.77) * mm, "mid": v(63.4, 78.03) * mm, "end": v(68.55, 86.37) * mm});
            skLineSegment(sketch, "E353", {"start": v(50.06, 74.77) * mm, "end": v(54.16, 74.77) * mm});
            skLineSegment(sketch, "E354", {"start": v(50.06, 74.77) * mm, "end": v(50.06, 86.96) * mm});
            skLineSegment(sketch, "E355", {"start": v(50.06, 86.96) * mm, "end": v(54.23, 86.96) * mm});
            skArc(sketch, "E356", {"start": v(54.23, 86.96) * mm, "mid": v(55.66, 87.55) * mm, "end": v(56.26, 88.99) * mm});
            skArc(sketch, "E357", {"start": v(28.56, 85.36) * mm, "mid": v(31.66, 77.87) * mm, "end": v(39.15, 74.77) * mm});
            skLineSegment(sketch, "E358", {"start": v(28.56, 85.36) * mm, "end": v(28.56, 138.17) * mm});
            skArc(sketch, "E359", {"start": v(41.48, 144.13) * mm, "mid": v(33.7, 144.02) * mm, "end": v(28.56, 138.17) * mm});
            skLineSegment(sketch, "E360", {"start": v(41.48, 144.13) * mm, "end": v(46.88, 141.8) * mm});
            skLineSegment(sketch, "E361", {"start": v(46.88, 141.8) * mm, "end": v(46.88, 127.22) * mm});
            skLineSegment(sketch, "E362", {"start": v(44.08, 128.28) * mm, "end": v(46.88, 127.22) * mm});
            skArc(sketch, "E363", {"start": v(44.08, 128.28) * mm, "mid": v(40.62, 127.77) * mm, "end": v(39.02, 124.65) * mm});
            skLineSegment(sketch, "E364", {"start": v(39.02, 124.65) * mm, "end": v(39.02, 91.71) * mm});
            skArc(sketch, "E365", {"start": v(39.02, 91.71) * mm, "mid": v(40.4, 88.35) * mm, "end": v(43.77, 86.96) * mm});
            skLineSegment(sketch, "E366", {"start": v(43.77, 86.96) * mm, "end": v(46.88, 86.96) * mm});
            skLineSegment(sketch, "E367", {"start": v(46.88, 86.96) * mm, "end": v(46.88, 74.77) * mm});
            skLineSegment(sketch, "E368", {"start": v(39.15, 74.77) * mm, "end": v(46.88, 74.77) * mm});
            skArc(sketch, "E369", {"start": v(-35, 74.58) * mm, "mid": v(-29.26, 79.66) * mm, "end": v(-27.25, 87.06) * mm});
            skLineSegment(sketch, "E370", {"start": v(-35, 74.58) * mm, "end": v(-43.6, 74.46) * mm});
            skLineSegment(sketch, "E371", {"start": v(-43.6, 87.06) * mm, "end": v(-43.6, 74.46) * mm});
            skLineSegment(sketch, "E372", {"start": v(-40.7, 87.06) * mm, "end": v(-43.6, 87.06) * mm});
            skArc(sketch, "E373", {"start": v(-40.7, 87.06) * mm, "mid": v(-37.53, 87.91) * mm, "end": v(-36.15, 90.89) * mm});
            skLineSegment(sketch, "E374", {"start": v(-36.15, 123.9) * mm, "end": v(-36.15, 90.89) * mm});
            skArc(sketch, "E375", {"start": v(-36.15, 123.9) * mm, "mid": v(-37.97, 127.42) * mm, "end": v(-41.89, 127.97) * mm});
            skLineSegment(sketch, "E376", {"start": v(-43.6, 127.16) * mm, "end": v(-41.89, 127.97) * mm});
            skLineSegment(sketch, "E377", {"start": v(-43.6, 141.41) * mm, "end": v(-43.6, 127.16) * mm});
            skLineSegment(sketch, "E378", {"start": v(-36.83, 144.55) * mm, "end": v(-43.6, 141.41) * mm});
            skArc(sketch, "E379", {"start": v(-27.25, 135.57) * mm, "mid": v(-30.1, 142.13) * mm, "end": v(-36.83, 144.55) * mm});
            skLineSegment(sketch, "E380", {"start": v(-27.25, 135.57) * mm, "end": v(-27.25, 87.06) * mm});
            skLineSegment(sketch, "E381", {"start": v(6.76, -67.45) * mm, "end": v(6.76, -165.54) * mm});
            skLineSegment(sketch, "E382", {"start": v(6.76, -67.45) * mm, "end": v(20.65, -67.45) * mm});
            skLineSegment(sketch, "E383", {"start": v(20.65, -67.45) * mm, "end": v(20.65, -151.3) * mm});
            skLineSegment(sketch, "E384", {"start": v(34.56, -145.46) * mm, "end": v(20.65, -151.3) * mm});
            skLineSegment(sketch, "E385", {"start": v(34.56, -157.4) * mm, "end": v(34.56, -145.46) * mm});
            skLineSegment(sketch, "E386", {"start": v(11.29, -168.41) * mm, "end": v(34.56, -157.4) * mm});
            skArc(sketch, "E387", {"start": v(6.76, -165.54) * mm, "mid": v(8.23, -168.22) * mm, "end": v(11.29, -168.41) * mm});
            skArc(sketch, "E388", {"start": v(160.19, 28.65) * mm, "mid": v(145.25, 39.2) * mm, "end": v(131, 27.73) * mm});
            skLineSegment(sketch, "E389", {"start": v(160.19, 28.65) * mm, "end": v(160.19, 16.5) * mm});
            skLineSegment(sketch, "E390", {"start": v(160.19, 16.5) * mm, "end": v(150.76, 16.5) * mm});
            skLineSegment(sketch, "E391", {"start": v(150.76, 16.5) * mm, "end": v(150.76, 25.86) * mm});
            skArc(sketch, "E392", {"start": v(150.76, 25.86) * mm, "mid": v(145.93, 30.77) * mm, "end": v(141.02, 25.93) * mm});
            skLineSegment(sketch, "E393", {"start": v(141.02, 25.93) * mm, "end": v(141.05, 19.5) * mm});
            skArc(sketch, "E394", {"start": v(141.05, 19.5) * mm, "mid": v(141.57, 17) * mm, "end": v(143.03, 14.9) * mm});
            skLineSegment(sketch, "E395", {"start": v(143.03, 14.9) * mm, "end": v(159.34, -0.6) * mm});
            skArc(sketch, "E396", {"start": v(160.33, -2.9) * mm, "mid": v(160.07, -1.65) * mm, "end": v(159.34, -0.6) * mm});
            skLineSegment(sketch, "E397", {"start": v(160.33, -2.9) * mm, "end": v(160.1, -18.1) * mm});
            skArc(sketch, "E398", {"start": v(131.23, -22.28) * mm, "mid": v(147.44, -32.5) * mm, "end": v(160.1, -18.1) * mm});
            skLineSegment(sketch, "E399", {"start": v(131.23, -6.13) * mm, "end": v(131.23, -22.28) * mm});
            skLineSegment(sketch, "E400", {"start": v(141.37, -6.13) * mm, "end": v(131.23, -6.13) * mm});
            skLineSegment(sketch, "E401", {"start": v(141.37, -6.13) * mm, "end": v(142.1, -19.9) * mm});
            skArc(sketch, "E402", {"start": v(142.1, -19.9) * mm, "mid": v(146.38, -23.85) * mm, "end": v(150.43, -19.68) * mm});
            skLineSegment(sketch, "E403", {"start": v(150.43, -19.68) * mm, "end": v(150.43, -10.54) * mm});
            skArc(sketch, "E404", {"start": v(150.43, -10.54) * mm, "mid": v(150.07, -8.3) * mm, "end": v(148.95, -6.33) * mm});
            skLineSegment(sketch, "E405", {"start": v(133, 8.76) * mm, "end": v(148.95, -6.33) * mm});
            skArc(sketch, "E406", {"start": v(131, 13.38) * mm, "mid": v(131.52, 10.87) * mm, "end": v(133, 8.76) * mm});
            skLineSegment(sketch, "E407", {"start": v(131, 27.73) * mm, "end": v(131, 13.38) * mm});
            skArc(sketch, "E408", {"start": v(195.99, 23.88) * mm, "mid": v(192.07, 34.15) * mm, "end": v(182.3, 39.2) * mm});
            skLineSegment(sketch, "E409", {"start": v(195.99, 23.88) * mm, "end": v(195.99, -19.41) * mm});
            skArc(sketch, "E410", {"start": v(182.3, -32.66) * mm, "mid": v(191.5, -28.46) * mm, "end": v(195.99, -19.41) * mm});
            skLineSegment(sketch, "E411", {"start": v(182.3, -32.66) * mm, "end": v(182.3, -22.05) * mm});
            skArc(sketch, "E412", {"start": v(182.3, -22.05) * mm, "mid": v(184.6, -20.53) * mm, "end": v(185.69, -18) * mm});
            skLineSegment(sketch, "E413", {"start": v(185.25, 24.6) * mm, "end": v(185.69, -18) * mm});
            skArc(sketch, "E414", {"start": v(185.25, 24.6) * mm, "mid": v(184.42, 27.01) * mm, "end": v(182.3, 28.43) * mm});
            skLineSegment(sketch, "E415", {"start": v(182.3, 28.43) * mm, "end": v(182.3, 39.2) * mm});
            skArc(sketch, "E416", {"start": v(12.46, 28.12) * mm, "mid": v(9.07, 36.57) * mm, "end": v(0.78, 40.34) * mm});
            skLineSegment(sketch, "E417", {"start": v(12.46, 28.12) * mm, "end": v(12.46, -19.78) * mm});
            skArc(sketch, "E418", {"start": v(0.4, -31.85) * mm, "mid": v(8.93, -28.31) * mm, "end": v(12.46, -19.78) * mm});
            skLineSegment(sketch, "E419", {"start": v(-0.86, -31.85) * mm, "end": v(0.4, -31.85) * mm});
            skLineSegment(sketch, "E420", {"start": v(-0.86, -31.85) * mm, "end": v(-0.86, -20.77) * mm});
            skArc(sketch, "E421", {"start": v(-0.86, -20.77) * mm, "mid": v(0.99, -20) * mm, "end": v(1.75, -18.16) * mm});
            skLineSegment(sketch, "E422", {"start": v(1.75, 26.77) * mm, "end": v(1.75, -18.16) * mm});
            skArc(sketch, "E423", {"start": v(1.75, 26.77) * mm, "mid": v(0.99, 28.62) * mm, "end": v(-0.86, 29.38) * mm});
            skLineSegment(sketch, "E424", {"start": v(-0.86, 29.38) * mm, "end": v(-0.86, 40.34) * mm});
            skLineSegment(sketch, "E425", {"start": v(-0.86, 40.34) * mm, "end": v(0.78, 40.34) * mm});
            skLineSegment(sketch, "E426", {"start": v(-16.59, 40.34) * mm, "end": v(-16.59, -31.85) * mm});
            skLineSegment(sketch, "E427", {"start": v(-16.59, 40.34) * mm, "end": v(-4.04, 40.34) * mm});
            skLineSegment(sketch, "E428", {"start": v(-4.04, 40.34) * mm, "end": v(-4.04, 29.38) * mm});
            skLineSegment(sketch, "E429", {"start": v(-4.04, 29.38) * mm, "end": v(-4.89, 29.38) * mm});
            skLineSegment(sketch, "E430", {"start": v(-4.89, 29.38) * mm, "end": v(-4.89, -20.77) * mm});
            skLineSegment(sketch, "E431", {"start": v(-4.89, -20.77) * mm, "end": v(-4.04, -20.77) * mm});
            skLineSegment(sketch, "E432", {"start": v(-4.04, -20.77) * mm, "end": v(-4.04, -31.85) * mm});
            skLineSegment(sketch, "E433", {"start": v(-16.59, -31.85) * mm, "end": v(-4.04, -31.85) * mm});
            skLineSegment(sketch, "E434", {"start": v(0, 203.2) * mm, "end": v(14.14, 193.04) * mm});
            skLineSegment(sketch, "E435", {"start": v(0, 203.2) * mm, "end": v(-14.14, 193.04) * mm});
            skLineSegment(sketch, "E436", {"start": v(-14.14, 193.04) * mm, "end": v(-29.86, 183.18) * mm});
            skLineSegment(sketch, "E437", {"start": v(-29.86, 183.18) * mm, "end": v(-48.7, 173.93) * mm});
            skLineSegment(sketch, "E438", {"start": v(-48.7, 173.93) * mm, "end": v(-70.85, 165.63) * mm});
            skLineSegment(sketch, "E439", {"start": v(-70.85, 165.63) * mm, "end": v(-94.57, 158.69) * mm});
            skLineSegment(sketch, "E440", {"start": v(-94.57, 158.69) * mm, "end": v(-124.85, 152.3) * mm});
            skLineSegment(sketch, "E441", {"start": v(-124.85, 152.3) * mm, "end": v(-152.12, 149.07) * mm});
            skLineSegment(sketch, "E442", {"start": v(-152.12, 149.07) * mm, "end": v(-177.64, 147.51) * mm});
            skLineSegment(sketch, "E443", {"start": v(-177.64, 147.51) * mm, "end": v(-177.64, 95.93) * mm});
            skArc(sketch, "E444", {"start": v(-154.52, 75.09) * mm, "mid": v(-161.81, 90.24) * mm, "end": v(-177.64, 95.93) * mm});
            skLineSegment(sketch, "E445", {"start": v(-154.52, 75.09) * mm, "end": v(-269.23, 75.09) * mm});
            skLineSegment(sketch, "E446", {"start": v(-269.23, 75.09) * mm, "end": v(-269.23, -67.6) * mm});
            skLineSegment(sketch, "E447", {"start": v(-269.23, -67.6) * mm, "end": v(-162.44, -67.6) * mm});
            skLineSegment(sketch, "E448", {"start": v(-162.44, -67.6) * mm, "end": v(-163.66, -72.73) * mm});
            skLineSegment(sketch, "E449", {"start": v(-163.66, -72.73) * mm, "end": v(-166.82, -77.61) * mm});
            skLineSegment(sketch, "E450", {"start": v(-166.82, -77.61) * mm, "end": v(-172.82, -81.94) * mm});
            skLineSegment(sketch, "E451", {"start": v(-172.82, -81.94) * mm, "end": v(-178.85, -84.51) * mm});
            skLineSegment(sketch, "E452", {"start": v(-178.85, -84.51) * mm, "end": v(-185.72, -86.3) * mm});
            skLineSegment(sketch, "E453", {"start": v(-185.72, -86.3) * mm, "end": v(-190.42, -87.13) * mm});
            skLineSegment(sketch, "E454", {"start": v(-190.42, -87.13) * mm, "end": v(-193.55, -87.56) * mm});
            skLineSegment(sketch, "E455", {"start": v(-193.55, -87.56) * mm, "end": v(-194.2, -87.64) * mm});
            skLineSegment(sketch, "E456", {"start": v(-194.2, -87.64) * mm, "end": v(-194.24, -87.65) * mm});
            skLineSegment(sketch, "E457", {"start": v(-194.24, -87.65) * mm, "end": v(-194.24, -87.65) * mm});
            skLineSegment(sketch, "E458", {"start": v(-181.11, -99.14) * mm, "end": v(-194.24, -87.65) * mm});
            skLineSegment(sketch, "E459", {"start": v(-166.27, -111.63) * mm, "end": v(-181.11, -99.14) * mm});
            skLineSegment(sketch, "E460", {"start": v(-148.88, -125.45) * mm, "end": v(-166.27, -111.63) * mm});
            skLineSegment(sketch, "E461", {"start": v(-128.52, -140.67) * mm, "end": v(-148.88, -125.45) * mm});
            skLineSegment(sketch, "E462", {"start": v(-106.3, -156.26) * mm, "end": v(-128.52, -140.67) * mm});
            skLineSegment(sketch, "E463", {"start": v(-85.78, -169.67) * mm, "end": v(-106.3, -156.26) * mm});
            skLineSegment(sketch, "E464", {"start": v(-66.15, -181.35) * mm, "end": v(-85.78, -169.67) * mm});
            skLineSegment(sketch, "E465", {"start": v(-48.46, -190.42) * mm, "end": v(-66.15, -181.35) * mm});
            skLineSegment(sketch, "E466", {"start": v(-33.08, -196.81) * mm, "end": v(-48.46, -190.42) * mm});
            skLineSegment(sketch, "E467", {"start": v(-20.07, -200.75) * mm, "end": v(-33.08, -196.81) * mm});
            skLineSegment(sketch, "E468", {"start": v(-9.37, -202.56) * mm, "end": v(-20.07, -200.75) * mm});
            skLineSegment(sketch, "E469", {"start": v(0, -203.2) * mm, "end": v(-9.37, -202.56) * mm});
            skLineSegment(sketch, "E470", {"start": v(0, -203.2) * mm, "end": v(9.37, -202.56) * mm});
            skLineSegment(sketch, "E471", {"start": v(9.37, -202.56) * mm, "end": v(20.07, -200.75) * mm});
            skLineSegment(sketch, "E472", {"start": v(20.07, -200.75) * mm, "end": v(33.08, -196.81) * mm});
            skLineSegment(sketch, "E473", {"start": v(33.08, -196.81) * mm, "end": v(48.46, -190.42) * mm});
            skLineSegment(sketch, "E474", {"start": v(48.46, -190.42) * mm, "end": v(66.15, -181.35) * mm});
            skLineSegment(sketch, "E475", {"start": v(66.15, -181.35) * mm, "end": v(85.78, -169.67) * mm});
            skLineSegment(sketch, "E476", {"start": v(85.78, -169.67) * mm, "end": v(106.3, -156.26) * mm});
            skLineSegment(sketch, "E477", {"start": v(106.3, -156.26) * mm, "end": v(128.52, -140.67) * mm});
            skLineSegment(sketch, "E478", {"start": v(128.52, -140.67) * mm, "end": v(148.88, -125.45) * mm});
            skLineSegment(sketch, "E479", {"start": v(148.88, -125.45) * mm, "end": v(166.27, -111.63) * mm});
            skLineSegment(sketch, "E480", {"start": v(166.27, -111.63) * mm, "end": v(181.11, -99.14) * mm});
            skLineSegment(sketch, "E481", {"start": v(181.11, -99.14) * mm, "end": v(194.24, -87.65) * mm});
            skLineSegment(sketch, "E482", {"start": v(194.24, -87.65) * mm, "end": v(194.24, -87.65) * mm});
            skLineSegment(sketch, "E483", {"start": v(194.2, -87.64) * mm, "end": v(194.24, -87.65) * mm});
            skLineSegment(sketch, "E484", {"start": v(193.55, -87.56) * mm, "end": v(194.2, -87.64) * mm});
            skLineSegment(sketch, "E485", {"start": v(190.42, -87.13) * mm, "end": v(193.55, -87.56) * mm});
            skLineSegment(sketch, "E486", {"start": v(185.72, -86.3) * mm, "end": v(190.42, -87.13) * mm});
            skLineSegment(sketch, "E487", {"start": v(178.85, -84.51) * mm, "end": v(185.72, -86.3) * mm});
            skLineSegment(sketch, "E488", {"start": v(172.82, -81.94) * mm, "end": v(178.85, -84.51) * mm});
            skLineSegment(sketch, "E489", {"start": v(166.82, -77.61) * mm, "end": v(172.82, -81.94) * mm});
            skLineSegment(sketch, "E490", {"start": v(163.66, -72.73) * mm, "end": v(166.82, -77.61) * mm});
            skLineSegment(sketch, "E491", {"start": v(162.44, -67.6) * mm, "end": v(163.66, -72.73) * mm});
            skLineSegment(sketch, "E492", {"start": v(269.23, -67.6) * mm, "end": v(162.44, -67.6) * mm});
            skLineSegment(sketch, "E493", {"start": v(269.23, 75.09) * mm, "end": v(269.23, -67.6) * mm});
            skLineSegment(sketch, "E494", {"start": v(154.52, 75.09) * mm, "end": v(269.23, 75.09) * mm});
            skArc(sketch, "E495", {"start": v(154.52, 75.09) * mm, "mid": v(161.81, 90.24) * mm, "end": v(177.64, 95.93) * mm});
            skLineSegment(sketch, "E496", {"start": v(177.64, 147.51) * mm, "end": v(177.64, 95.93) * mm});
            skLineSegment(sketch, "E497", {"start": v(152.12, 149.07) * mm, "end": v(177.64, 147.51) * mm});
            skLineSegment(sketch, "E498", {"start": v(124.85, 152.3) * mm, "end": v(152.12, 149.07) * mm});
            skLineSegment(sketch, "E499", {"start": v(94.57, 158.69) * mm, "end": v(124.85, 152.3) * mm});
            skLineSegment(sketch, "E500", {"start": v(70.85, 165.63) * mm, "end": v(94.57, 158.69) * mm});
            skLineSegment(sketch, "E501", {"start": v(48.7, 173.93) * mm, "end": v(70.85, 165.63) * mm});
            skLineSegment(sketch, "E502", {"start": v(29.86, 183.18) * mm, "end": v(48.7, 173.93) * mm});
            skLineSegment(sketch, "E503", {"start": v(14.14, 193.04) * mm, "end": v(29.86, 183.18) * mm});
            skSolve(sketch);
        }
        {
            var Q0;
            Q0=makeQuery(id+"F0.imprint","IMPRINT",FACE,{"disambiguationData":[TD([[makeQuery(id+"F0.imprint","IMPRINT",EDGE,{"derivedFrom":sQuery(id+"F0.wireOp",EDGE,"E0")}),-1.0]])]});
            extrude(context, id + "F1", {"entities" : qUnion([Q0]), "depth" : 3.17 * mm});
        }
        {
            var Q0;
            Q0=makeQuery(id+"F1.opExtrude","CAP_FACE",FACE,{"disambiguationData":[OSD([sQuery(id+"F0.wireOp",EDGE,"E0"),sQuery(id+"F0.wireOp",EDGE,"E1"),sQuery(id+"F0.wireOp",EDGE,"E2"),sQuery(id+"F0.wireOp",EDGE,"E3"),sQuery(id+"F0.wireOp",EDGE,"E4"),sQuery(id+"F0.wireOp",EDGE,"E5"),sQuery(id+"F0.wireOp",EDGE,"E6"),sQuery(id+"F0.wireOp",EDGE,"E7"),sQuery(id+"F0.wireOp",EDGE,"E8"),sQuery(id+"F0.wireOp",EDGE,"E9"),sQuery(id+"F0.wireOp",EDGE,"E10"),sQuery(id+"F0.wireOp",EDGE,"E11"),sQuery(id+"F0.wireOp",EDGE,"E12"),sQuery(id+"F0.wireOp",EDGE,"E13"),sQuery(id+"F0.wireOp",EDGE,"E14"),sQuery(id+"F0.wireOp",EDGE,"E15"),sQuery(id+"F0.wireOp",EDGE,"E16"),sQuery(id+"F0.wireOp",EDGE,"E17"),sQuery(id+"F0.wireOp",EDGE,"E18"),sQuery(id+"F0.wireOp",EDGE,"E19"),sQuery(id+"F0.wireOp",EDGE,"E20"),sQuery(id+"F0.wireOp",EDGE,"E21"),sQuery(id+"F0.wireOp",EDGE,"E22"),sQuery(id+"F0.wireOp",EDGE,"E23"),sQuery(id+"F0.wireOp",EDGE,"E24"),sQuery(id+"F0.wireOp",EDGE,"E25"),sQuery(id+"F0.wireOp",EDGE,"E26"),sQuery(id+"F0.wireOp",EDGE,"E27"),sQuery(id+"F0.wireOp",EDGE,"E28"),sQuery(id+"F0.wireOp",EDGE,"E29"),sQuery(id+"F0.wireOp",EDGE,"E30"),sQuery(id+"F0.wireOp",EDGE,"E31"),sQuery(id+"F0.wireOp",EDGE,"E32"),sQuery(id+"F0.wireOp",EDGE,"E33"),sQuery(id+"F0.wireOp",EDGE,"E34"),sQuery(id+"F0.wireOp",EDGE,"E35"),sQuery(id+"F0.wireOp",EDGE,"E36"),sQuery(id+"F0.wireOp",EDGE,"E37"),sQuery(id+"F0.wireOp",EDGE,"E38"),sQuery(id+"F0.wireOp",EDGE,"E39"),sQuery(id+"F0.wireOp",EDGE,"E40"),sQuery(id+"F0.wireOp",EDGE,"E41"),sQuery(id+"F0.wireOp",EDGE,"E42"),sQuery(id+"F0.wireOp",EDGE,"E43"),sQuery(id+"F0.wireOp",EDGE,"E44"),sQuery(id+"F0.wireOp",EDGE,"E45"),sQuery(id+"F0.wireOp",EDGE,"E46"),sQuery(id+"F0.wireOp",EDGE,"E47"),sQuery(id+"F0.wireOp",EDGE,"E48"),sQuery(id+"F0.wireOp",EDGE,"E49"),sQuery(id+"F0.wireOp",EDGE,"E50"),sQuery(id+"F0.wireOp",EDGE,"E51"),sQuery(id+"F0.wireOp",EDGE,"E52"),sQuery(id+"F0.wireOp",EDGE,"E53"),sQuery(id+"F0.wireOp",EDGE,"E54"),sQuery(id+"F0.wireOp",EDGE,"E55"),sQuery(id+"F0.wireOp",EDGE,"E56"),sQuery(id+"F0.wireOp",EDGE,"E57"),sQuery(id+"F0.wireOp",EDGE,"E58"),sQuery(id+"F0.wireOp",EDGE,"E59"),sQuery(id+"F0.wireOp",EDGE,"E60"),sQuery(id+"F0.wireOp",EDGE,"E61"),sQuery(id+"F0.wireOp",EDGE,"E62"),sQuery(id+"F0.wireOp",EDGE,"E63"),sQuery(id+"F0.wireOp",EDGE,"E64"),sQuery(id+"F0.wireOp",EDGE,"E65"),sQuery(id+"F0.wireOp",EDGE,"E66"),sQuery(id+"F0.wireOp",EDGE,"E67"),sQuery(id+"F0.wireOp",EDGE,"E68"),sQuery(id+"F0.wireOp",EDGE,"E69"),sQuery(id+"F0.wireOp",EDGE,"E70"),sQuery(id+"F0.wireOp",EDGE,"E71"),sQuery(id+"F0.wireOp",EDGE,"E72"),sQuery(id+"F0.wireOp",EDGE,"E73"),sQuery(id+"F0.wireOp",EDGE,"E74"),sQuery(id+"F0.wireOp",EDGE,"E75"),sQuery(id+"F0.wireOp",EDGE,"E76"),sQuery(id+"F0.wireOp",EDGE,"E77"),sQuery(id+"F0.wireOp",EDGE,"E78"),sQuery(id+"F0.wireOp",EDGE,"E79"),sQuery(id+"F0.wireOp",EDGE,"E80"),sQuery(id+"F0.wireOp",EDGE,"E81"),sQuery(id+"F0.wireOp",EDGE,"E82"),sQuery(id+"F0.wireOp",EDGE,"E83"),sQuery(id+"F0.wireOp",EDGE,"E84"),sQuery(id+"F0.wireOp",EDGE,"E85"),sQuery(id+"F0.wireOp",EDGE,"E86"),sQuery(id+"F0.wireOp",EDGE,"E87"),sQuery(id+"F0.wireOp",EDGE,"E88"),sQuery(id+"F0.wireOp",EDGE,"E89"),sQuery(id+"F0.wireOp",EDGE,"E90"),sQuery(id+"F0.wireOp",EDGE,"E91"),sQuery(id+"F0.wireOp",EDGE,"E92"),sQuery(id+"F0.wireOp",EDGE,"E93"),sQuery(id+"F0.wireOp",EDGE,"E94"),sQuery(id+"F0.wireOp",EDGE,"E95"),sQuery(id+"F0.wireOp",EDGE,"E96"),sQuery(id+"F0.wireOp",EDGE,"E97"),sQuery(id+"F0.wireOp",EDGE,"E98"),sQuery(id+"F0.wireOp",EDGE,"E99"),sQuery(id+"F0.wireOp",EDGE,"E100"),sQuery(id+"F0.wireOp",EDGE,"E101"),sQuery(id+"F0.wireOp",EDGE,"E102"),sQuery(id+"F0.wireOp",EDGE,"E103"),sQuery(id+"F0.wireOp",EDGE,"E104"),sQuery(id+"F0.wireOp",EDGE,"E105"),sQuery(id+"F0.wireOp",EDGE,"E106"),sQuery(id+"F0.wireOp",EDGE,"E107"),sQuery(id+"F0.wireOp",EDGE,"E108"),sQuery(id+"F0.wireOp",EDGE,"E109"),sQuery(id+"F0.wireOp",EDGE,"E110"),sQuery(id+"F0.wireOp",EDGE,"E111"),sQuery(id+"F0.wireOp",EDGE,"E112"),sQuery(id+"F0.wireOp",EDGE,"E113"),sQuery(id+"F0.wireOp",EDGE,"E114"),sQuery(id+"F0.wireOp",EDGE,"E115"),sQuery(id+"F0.wireOp",EDGE,"E116"),sQuery(id+"F0.wireOp",EDGE,"E117"),sQuery(id+"F0.wireOp",EDGE,"E118"),sQuery(id+"F0.wireOp",EDGE,"E119"),sQuery(id+"F0.wireOp",EDGE,"E120"),sQuery(id+"F0.wireOp",EDGE,"E121"),sQuery(id+"F0.wireOp",EDGE,"E122"),sQuery(id+"F0.wireOp",EDGE,"E123"),sQuery(id+"F0.wireOp",EDGE,"E124"),sQuery(id+"F0.wireOp",EDGE,"E125"),sQuery(id+"F0.wireOp",EDGE,"E126"),sQuery(id+"F0.wireOp",EDGE,"E127"),sQuery(id+"F0.wireOp",EDGE,"E128"),sQuery(id+"F0.wireOp",EDGE,"E129"),sQuery(id+"F0.wireOp",EDGE,"E130"),sQuery(id+"F0.wireOp",EDGE,"E131"),sQuery(id+"F0.wireOp",EDGE,"E132"),sQuery(id+"F0.wireOp",EDGE,"E133"),sQuery(id+"F0.wireOp",EDGE,"E134"),sQuery(id+"F0.wireOp",EDGE,"E135"),sQuery(id+"F0.wireOp",EDGE,"E136"),sQuery(id+"F0.wireOp",EDGE,"E137"),sQuery(id+"F0.wireOp",EDGE,"E138"),sQuery(id+"F0.wireOp",EDGE,"E139"),sQuery(id+"F0.wireOp",EDGE,"E140"),sQuery(id+"F0.wireOp",EDGE,"E141"),sQuery(id+"F0.wireOp",EDGE,"E142"),sQuery(id+"F0.wireOp",EDGE,"E143"),sQuery(id+"F0.wireOp",EDGE,"E144"),sQuery(id+"F0.wireOp",EDGE,"E145"),sQuery(id+"F0.wireOp",EDGE,"E146"),sQuery(id+"F0.wireOp",EDGE,"E147"),sQuery(id+"F0.wireOp",EDGE,"E148"),sQuery(id+"F0.wireOp",EDGE,"E149"),sQuery(id+"F0.wireOp",EDGE,"E150"),sQuery(id+"F0.wireOp",EDGE,"E151"),sQuery(id+"F0.wireOp",EDGE,"E152"),sQuery(id+"F0.wireOp",EDGE,"E153"),sQuery(id+"F0.wireOp",EDGE,"E154"),sQuery(id+"F0.wireOp",EDGE,"E155"),sQuery(id+"F0.wireOp",EDGE,"E156"),sQuery(id+"F0.wireOp",EDGE,"E157"),sQuery(id+"F0.wireOp",EDGE,"E158"),sQuery(id+"F0.wireOp",EDGE,"E159"),sQuery(id+"F0.wireOp",EDGE,"E160"),sQuery(id+"F0.wireOp",EDGE,"E161"),sQuery(id+"F0.wireOp",EDGE,"E162"),sQuery(id+"F0.wireOp",EDGE,"E163"),sQuery(id+"F0.wireOp",EDGE,"E164"),sQuery(id+"F0.wireOp",EDGE,"E165"),sQuery(id+"F0.wireOp",EDGE,"E166"),sQuery(id+"F0.wireOp",EDGE,"E167"),sQuery(id+"F0.wireOp",EDGE,"E168"),sQuery(id+"F0.wireOp",EDGE,"E169"),sQuery(id+"F0.wireOp",EDGE,"E170"),sQuery(id+"F0.wireOp",EDGE,"E171"),sQuery(id+"F0.wireOp",EDGE,"E172"),sQuery(id+"F0.wireOp",EDGE,"E173"),sQuery(id+"F0.wireOp",EDGE,"E174"),sQuery(id+"F0.wireOp",EDGE,"E175"),sQuery(id+"F0.wireOp",EDGE,"E176"),sQuery(id+"F0.wireOp",EDGE,"E177"),sQuery(id+"F0.wireOp",EDGE,"E178"),sQuery(id+"F0.wireOp",EDGE,"E179"),sQuery(id+"F0.wireOp",EDGE,"E180"),sQuery(id+"F0.wireOp",EDGE,"E181"),sQuery(id+"F0.wireOp",EDGE,"E182"),sQuery(id+"F0.wireOp",EDGE,"E183"),sQuery(id+"F0.wireOp",EDGE,"E184"),sQuery(id+"F0.wireOp",EDGE,"E185"),sQuery(id+"F0.wireOp",EDGE,"E186"),sQuery(id+"F0.wireOp",EDGE,"E187"),sQuery(id+"F0.wireOp",EDGE,"E188"),sQuery(id+"F0.wireOp",EDGE,"E189"),sQuery(id+"F0.wireOp",EDGE,"E190"),sQuery(id+"F0.wireOp",EDGE,"E191"),sQuery(id+"F0.wireOp",EDGE,"E192"),sQuery(id+"F0.wireOp",EDGE,"E193"),sQuery(id+"F0.wireOp",EDGE,"E194"),sQuery(id+"F0.wireOp",EDGE,"E195"),sQuery(id+"F0.wireOp",EDGE,"E196"),sQuery(id+"F0.wireOp",EDGE,"E197"),sQuery(id+"F0.wireOp",EDGE,"E198"),sQuery(id+"F0.wireOp",EDGE,"E199"),sQuery(id+"F0.wireOp",EDGE,"E200"),sQuery(id+"F0.wireOp",EDGE,"E201"),sQuery(id+"F0.wireOp",EDGE,"E202"),sQuery(id+"F0.wireOp",EDGE,"E203"),sQuery(id+"F0.wireOp",EDGE,"E204"),sQuery(id+"F0.wireOp",EDGE,"E205"),sQuery(id+"F0.wireOp",EDGE,"E206"),sQuery(id+"F0.wireOp",EDGE,"E207"),sQuery(id+"F0.wireOp",EDGE,"E208"),sQuery(id+"F0.wireOp",EDGE,"E209"),sQuery(id+"F0.wireOp",EDGE,"E210"),sQuery(id+"F0.wireOp",EDGE,"E211"),sQuery(id+"F0.wireOp",EDGE,"E212"),sQuery(id+"F0.wireOp",EDGE,"E213"),sQuery(id+"F0.wireOp",EDGE,"E214"),sQuery(id+"F0.wireOp",EDGE,"E215"),sQuery(id+"F0.wireOp",EDGE,"E216"),sQuery(id+"F0.wireOp",EDGE,"E217"),sQuery(id+"F0.wireOp",EDGE,"E218"),sQuery(id+"F0.wireOp",EDGE,"E219"),sQuery(id+"F0.wireOp",EDGE,"E220"),sQuery(id+"F0.wireOp",EDGE,"E221"),sQuery(id+"F0.wireOp",EDGE,"E222"),sQuery(id+"F0.wireOp",EDGE,"E223"),sQuery(id+"F0.wireOp",EDGE,"E224"),sQuery(id+"F0.wireOp",EDGE,"E225"),sQuery(id+"F0.wireOp",EDGE,"E226"),sQuery(id+"F0.wireOp",EDGE,"E227"),sQuery(id+"F0.wireOp",EDGE,"E228"),sQuery(id+"F0.wireOp",EDGE,"E229"),sQuery(id+"F0.wireOp",EDGE,"E230"),sQuery(id+"F0.wireOp",EDGE,"E231"),sQuery(id+"F0.wireOp",EDGE,"E232"),sQuery(id+"F0.wireOp",EDGE,"E233"),sQuery(id+"F0.wireOp",EDGE,"E234"),sQuery(id+"F0.wireOp",EDGE,"E235"),sQuery(id+"F0.wireOp",EDGE,"E236"),sQuery(id+"F0.wireOp",EDGE,"E237"),sQuery(id+"F0.wireOp",EDGE,"E238"),sQuery(id+"F0.wireOp",EDGE,"E239"),sQuery(id+"F0.wireOp",EDGE,"E240"),sQuery(id+"F0.wireOp",EDGE,"E241"),sQuery(id+"F0.wireOp",EDGE,"E242"),sQuery(id+"F0.wireOp",EDGE,"E243"),sQuery(id+"F0.wireOp",EDGE,"E244"),sQuery(id+"F0.wireOp",EDGE,"E245"),sQuery(id+"F0.wireOp",EDGE,"E246"),sQuery(id+"F0.wireOp",EDGE,"E247"),sQuery(id+"F0.wireOp",EDGE,"E248"),sQuery(id+"F0.wireOp",EDGE,"E249"),sQuery(id+"F0.wireOp",EDGE,"E250"),sQuery(id+"F0.wireOp",EDGE,"E251"),sQuery(id+"F0.wireOp",EDGE,"E252"),sQuery(id+"F0.wireOp",EDGE,"E253"),sQuery(id+"F0.wireOp",EDGE,"E254"),sQuery(id+"F0.wireOp",EDGE,"E255"),sQuery(id+"F0.wireOp",EDGE,"E256"),sQuery(id+"F0.wireOp",EDGE,"E257"),sQuery(id+"F0.wireOp",EDGE,"E258"),sQuery(id+"F0.wireOp",EDGE,"E259"),sQuery(id+"F0.wireOp",EDGE,"E260"),sQuery(id+"F0.wireOp",EDGE,"E261"),sQuery(id+"F0.wireOp",EDGE,"E262"),sQuery(id+"F0.wireOp",EDGE,"E263"),sQuery(id+"F0.wireOp",EDGE,"E264"),sQuery(id+"F0.wireOp",EDGE,"E265"),sQuery(id+"F0.wireOp",EDGE,"E266"),sQuery(id+"F0.wireOp",EDGE,"E267"),sQuery(id+"F0.wireOp",EDGE,"E268"),sQuery(id+"F0.wireOp",EDGE,"E269"),sQuery(id+"F0.wireOp",EDGE,"E270"),sQuery(id+"F0.wireOp",EDGE,"E271"),sQuery(id+"F0.wireOp",EDGE,"E272"),sQuery(id+"F0.wireOp",EDGE,"E273"),sQuery(id+"F0.wireOp",EDGE,"E274"),sQuery(id+"F0.wireOp",EDGE,"E275"),sQuery(id+"F0.wireOp",EDGE,"E276"),sQuery(id+"F0.wireOp",EDGE,"E277"),sQuery(id+"F0.wireOp",EDGE,"E278"),sQuery(id+"F0.wireOp",EDGE,"E279"),sQuery(id+"F0.wireOp",EDGE,"E280"),sQuery(id+"F0.wireOp",EDGE,"E281"),sQuery(id+"F0.wireOp",EDGE,"E282"),sQuery(id+"F0.wireOp",EDGE,"E283"),sQuery(id+"F0.wireOp",EDGE,"E284"),sQuery(id+"F0.wireOp",EDGE,"E285"),sQuery(id+"F0.wireOp",EDGE,"E286"),sQuery(id+"F0.wireOp",EDGE,"E287"),sQuery(id+"F0.wireOp",EDGE,"E288"),sQuery(id+"F0.wireOp",EDGE,"E289"),sQuery(id+"F0.wireOp",EDGE,"E290"),sQuery(id+"F0.wireOp",EDGE,"E291"),sQuery(id+"F0.wireOp",EDGE,"E292"),sQuery(id+"F0.wireOp",EDGE,"E293"),sQuery(id+"F0.wireOp",EDGE,"E294"),sQuery(id+"F0.wireOp",EDGE,"E295"),sQuery(id+"F0.wireOp",EDGE,"E296"),sQuery(id+"F0.wireOp",EDGE,"E297"),sQuery(id+"F0.wireOp",EDGE,"E298"),sQuery(id+"F0.wireOp",EDGE,"E299"),sQuery(id+"F0.wireOp",EDGE,"E300"),sQuery(id+"F0.wireOp",EDGE,"E301"),sQuery(id+"F0.wireOp",EDGE,"E302"),sQuery(id+"F0.wireOp",EDGE,"E303"),sQuery(id+"F0.wireOp",EDGE,"E304"),sQuery(id+"F0.wireOp",EDGE,"E305"),sQuery(id+"F0.wireOp",EDGE,"E306"),sQuery(id+"F0.wireOp",EDGE,"E307"),sQuery(id+"F0.wireOp",EDGE,"E308"),sQuery(id+"F0.wireOp",EDGE,"E309"),sQuery(id+"F0.wireOp",EDGE,"E310"),sQuery(id+"F0.wireOp",EDGE,"E311"),sQuery(id+"F0.wireOp",EDGE,"E312"),sQuery(id+"F0.wireOp",EDGE,"E313"),sQuery(id+"F0.wireOp",EDGE,"E314"),sQuery(id+"F0.wireOp",EDGE,"E315"),sQuery(id+"F0.wireOp",EDGE,"E316"),sQuery(id+"F0.wireOp",EDGE,"E317"),sQuery(id+"F0.wireOp",EDGE,"E318"),sQuery(id+"F0.wireOp",EDGE,"E319"),sQuery(id+"F0.wireOp",EDGE,"E320"),sQuery(id+"F0.wireOp",EDGE,"E321"),sQuery(id+"F0.wireOp",EDGE,"E322"),sQuery(id+"F0.wireOp",EDGE,"E323"),sQuery(id+"F0.wireOp",EDGE,"E324"),sQuery(id+"F0.wireOp",EDGE,"E325"),sQuery(id+"F0.wireOp",EDGE,"E326"),sQuery(id+"F0.wireOp",EDGE,"E327"),sQuery(id+"F0.wireOp",EDGE,"E328"),sQuery(id+"F0.wireOp",EDGE,"E329"),sQuery(id+"F0.wireOp",EDGE,"E330"),sQuery(id+"F0.wireOp",EDGE,"E331"),sQuery(id+"F0.wireOp",EDGE,"E332"),sQuery(id+"F0.wireOp",EDGE,"E333"),sQuery(id+"F0.wireOp",EDGE,"E334"),sQuery(id+"F0.wireOp",EDGE,"E335"),sQuery(id+"F0.wireOp",EDGE,"E336"),sQuery(id+"F0.wireOp",EDGE,"E337"),sQuery(id+"F0.wireOp",EDGE,"E338"),sQuery(id+"F0.wireOp",EDGE,"E339"),sQuery(id+"F0.wireOp",EDGE,"E340"),sQuery(id+"F0.wireOp",EDGE,"E341"),sQuery(id+"F0.wireOp",EDGE,"E342"),sQuery(id+"F0.wireOp",EDGE,"E343"),sQuery(id+"F0.wireOp",EDGE,"E344"),sQuery(id+"F0.wireOp",EDGE,"E345"),sQuery(id+"F0.wireOp",EDGE,"E346"),sQuery(id+"F0.wireOp",EDGE,"E347"),sQuery(id+"F0.wireOp",EDGE,"E348"),sQuery(id+"F0.wireOp",EDGE,"E349"),sQuery(id+"F0.wireOp",EDGE,"E350"),sQuery(id+"F0.wireOp",EDGE,"E351"),sQuery(id+"F0.wireOp",EDGE,"E352"),sQuery(id+"F0.wireOp",EDGE,"E353"),sQuery(id+"F0.wireOp",EDGE,"E354"),sQuery(id+"F0.wireOp",EDGE,"E355"),sQuery(id+"F0.wireOp",EDGE,"E356"),sQuery(id+"F0.wireOp",EDGE,"E357"),sQuery(id+"F0.wireOp",EDGE,"E358"),sQuery(id+"F0.wireOp",EDGE,"E359"),sQuery(id+"F0.wireOp",EDGE,"E360"),sQuery(id+"F0.wireOp",EDGE,"E361"),sQuery(id+"F0.wireOp",EDGE,"E362"),sQuery(id+"F0.wireOp",EDGE,"E363"),sQuery(id+"F0.wireOp",EDGE,"E364"),sQuery(id+"F0.wireOp",EDGE,"E365"),sQuery(id+"F0.wireOp",EDGE,"E366"),sQuery(id+"F0.wireOp",EDGE,"E367"),sQuery(id+"F0.wireOp",EDGE,"E368"),sQuery(id+"F0.wireOp",EDGE,"E369"),sQuery(id+"F0.wireOp",EDGE,"E370"),sQuery(id+"F0.wireOp",EDGE,"E371"),sQuery(id+"F0.wireOp",EDGE,"E372"),sQuery(id+"F0.wireOp",EDGE,"E373"),sQuery(id+"F0.wireOp",EDGE,"E374"),sQuery(id+"F0.wireOp",EDGE,"E375"),sQuery(id+"F0.wireOp",EDGE,"E376"),sQuery(id+"F0.wireOp",EDGE,"E377"),sQuery(id+"F0.wireOp",EDGE,"E378"),sQuery(id+"F0.wireOp",EDGE,"E379"),sQuery(id+"F0.wireOp",EDGE,"E380"),sQuery(id+"F0.wireOp",EDGE,"E381"),sQuery(id+"F0.wireOp",EDGE,"E382"),sQuery(id+"F0.wireOp",EDGE,"E383"),sQuery(id+"F0.wireOp",EDGE,"E384"),sQuery(id+"F0.wireOp",EDGE,"E385"),sQuery(id+"F0.wireOp",EDGE,"E386"),sQuery(id+"F0.wireOp",EDGE,"E387"),sQuery(id+"F0.wireOp",EDGE,"E388"),sQuery(id+"F0.wireOp",EDGE,"E389"),sQuery(id+"F0.wireOp",EDGE,"E390"),sQuery(id+"F0.wireOp",EDGE,"E391"),sQuery(id+"F0.wireOp",EDGE,"E392"),sQuery(id+"F0.wireOp",EDGE,"E393"),sQuery(id+"F0.wireOp",EDGE,"E394"),sQuery(id+"F0.wireOp",EDGE,"E395"),sQuery(id+"F0.wireOp",EDGE,"E396"),sQuery(id+"F0.wireOp",EDGE,"E397"),sQuery(id+"F0.wireOp",EDGE,"E398"),sQuery(id+"F0.wireOp",EDGE,"E399"),sQuery(id+"F0.wireOp",EDGE,"E400"),sQuery(id+"F0.wireOp",EDGE,"E401"),sQuery(id+"F0.wireOp",EDGE,"E402"),sQuery(id+"F0.wireOp",EDGE,"E403"),sQuery(id+"F0.wireOp",EDGE,"E404"),sQuery(id+"F0.wireOp",EDGE,"E405"),sQuery(id+"F0.wireOp",EDGE,"E406"),sQuery(id+"F0.wireOp",EDGE,"E407"),sQuery(id+"F0.wireOp",EDGE,"E408"),sQuery(id+"F0.wireOp",EDGE,"E409"),sQuery(id+"F0.wireOp",EDGE,"E410"),sQuery(id+"F0.wireOp",EDGE,"E411"),sQuery(id+"F0.wireOp",EDGE,"E412"),sQuery(id+"F0.wireOp",EDGE,"E413"),sQuery(id+"F0.wireOp",EDGE,"E414"),sQuery(id+"F0.wireOp",EDGE,"E415"),sQuery(id+"F0.wireOp",EDGE,"E416"),sQuery(id+"F0.wireOp",EDGE,"E417"),sQuery(id+"F0.wireOp",EDGE,"E418"),sQuery(id+"F0.wireOp",EDGE,"E419"),sQuery(id+"F0.wireOp",EDGE,"E420"),sQuery(id+"F0.wireOp",EDGE,"E421"),sQuery(id+"F0.wireOp",EDGE,"E422"),sQuery(id+"F0.wireOp",EDGE,"E423"),sQuery(id+"F0.wireOp",EDGE,"E424"),sQuery(id+"F0.wireOp",EDGE,"E425"),sQuery(id+"F0.wireOp",EDGE,"E426"),sQuery(id+"F0.wireOp",EDGE,"E427"),sQuery(id+"F0.wireOp",EDGE,"E428"),sQuery(id+"F0.wireOp",EDGE,"E429"),sQuery(id+"F0.wireOp",EDGE,"E430"),sQuery(id+"F0.wireOp",EDGE,"E431"),sQuery(id+"F0.wireOp",EDGE,"E432"),sQuery(id+"F0.wireOp",EDGE,"E433"),sQuery(id+"F0.wireOp",EDGE,"E434"),sQuery(id+"F0.wireOp",EDGE,"E435"),sQuery(id+"F0.wireOp",EDGE,"E436"),sQuery(id+"F0.wireOp",EDGE,"E437"),sQuery(id+"F0.wireOp",EDGE,"E438"),sQuery(id+"F0.wireOp",EDGE,"E439"),sQuery(id+"F0.wireOp",EDGE,"E440"),sQuery(id+"F0.wireOp",EDGE,"E441"),sQuery(id+"F0.wireOp",EDGE,"E442"),sQuery(id+"F0.wireOp",EDGE,"E443"),sQuery(id+"F0.wireOp",EDGE,"E444"),sQuery(id+"F0.wireOp",EDGE,"E445"),sQuery(id+"F0.wireOp",EDGE,"E446"),sQuery(id+"F0.wireOp",EDGE,"E447"),sQuery(id+"F0.wireOp",EDGE,"E448"),sQuery(id+"F0.wireOp",EDGE,"E449"),sQuery(id+"F0.wireOp",EDGE,"E450"),sQuery(id+"F0.wireOp",EDGE,"E451"),sQuery(id+"F0.wireOp",EDGE,"E452"),sQuery(id+"F0.wireOp",EDGE,"E453"),sQuery(id+"F0.wireOp",EDGE,"E454"),sQuery(id+"F0.wireOp",EDGE,"E455"),sQuery(id+"F0.wireOp",EDGE,"E456"),sQuery(id+"F0.wireOp",EDGE,"E457"),sQuery(id+"F0.wireOp",EDGE,"E458"),sQuery(id+"F0.wireOp",EDGE,"E459"),sQuery(id+"F0.wireOp",EDGE,"E460"),sQuery(id+"F0.wireOp",EDGE,"E461"),sQuery(id+"F0.wireOp",EDGE,"E462"),sQuery(id+"F0.wireOp",EDGE,"E463"),sQuery(id+"F0.wireOp",EDGE,"E464"),sQuery(id+"F0.wireOp",EDGE,"E465"),sQuery(id+"F0.wireOp",EDGE,"E466"),sQuery(id+"F0.wireOp",EDGE,"E467"),sQuery(id+"F0.wireOp",EDGE,"E468"),sQuery(id+"F0.wireOp",EDGE,"E469"),sQuery(id+"F0.wireOp",EDGE,"E470"),sQuery(id+"F0.wireOp",EDGE,"E471"),sQuery(id+"F0.wireOp",EDGE,"E472"),sQuery(id+"F0.wireOp",EDGE,"E473"),sQuery(id+"F0.wireOp",EDGE,"E474"),sQuery(id+"F0.wireOp",EDGE,"E475"),sQuery(id+"F0.wireOp",EDGE,"E476"),sQuery(id+"F0.wireOp",EDGE,"E477"),sQuery(id+"F0.wireOp",EDGE,"E478"),sQuery(id+"F0.wireOp",EDGE,"E479"),sQuery(id+"F0.wireOp",EDGE,"E480"),sQuery(id+"F0.wireOp",EDGE,"E481"),sQuery(id+"F0.wireOp",EDGE,"E482"),sQuery(id+"F0.wireOp",EDGE,"E482"),sQuery(id+"F0.wireOp",EDGE,"E483"),sQuery(id+"F0.wireOp",EDGE,"E484"),sQuery(id+"F0.wireOp",EDGE,"E485"),sQuery(id+"F0.wireOp",EDGE,"E486"),sQuery(id+"F0.wireOp",EDGE,"E487"),sQuery(id+"F0.wireOp",EDGE,"E488"),sQuery(id+"F0.wireOp",EDGE,"E489"),sQuery(id+"F0.wireOp",EDGE,"E490"),sQuery(id+"F0.wireOp",EDGE,"E491"),sQuery(id+"F0.wireOp",EDGE,"E492"),sQuery(id+"F0.wireOp",EDGE,"E493"),sQuery(id+"F0.wireOp",EDGE,"E494"),sQuery(id+"F0.wireOp",EDGE,"E495"),sQuery(id+"F0.wireOp",EDGE,"E496"),sQuery(id+"F0.wireOp",EDGE,"E497"),sQuery(id+"F0.wireOp",EDGE,"E498"),sQuery(id+"F0.wireOp",EDGE,"E499"),sQuery(id+"F0.wireOp",EDGE,"E500"),sQuery(id+"F0.wireOp",EDGE,"E501"),sQuery(id+"F0.wireOp",EDGE,"E502"),sQuery(id+"F0.wireOp",EDGE,"E503")])],"isStart":false});
            var sketch = newSketch(context, id + "F2", { "sketchPlane" : qUnion([Q0])});
            skLineSegment(sketch, "E504", {"start": v(0, 61.87) * mm, "end": v(0, 51.15) * mm, "construction": true});
            skLineSegment(sketch, "E505", {"start": v(0, -42.96) * mm, "end": v(0, -55.9) * mm, "construction": true});
            skArc(sketch, "E506.0.startCap", {"start": v(-3.98, 61.87) * mm, "mid": v(0, 65.84) * mm, "end": v(3.98, 61.87) * mm});
            skArc(sketch, "E506.0.endCap", {"start": v(3.98, 51.15) * mm, "mid": v(0, 47.18) * mm, "end": v(-3.98, 51.15) * mm});
            skLineSegment(sketch, "E506.0.left", {"start": v(3.98, 61.87) * mm, "end": v(3.98, 51.15) * mm});
            skLineSegment(sketch, "E506.0.right", {"start": v(-3.98, 61.87) * mm, "end": v(-3.98, 51.15) * mm});
            skArc(sketch, "E506.1.startCap", {"start": v(-3.98, -42.96) * mm, "mid": v(0, -38.99) * mm, "end": v(3.98, -42.96) * mm});
            skArc(sketch, "E506.1.endCap", {"start": v(3.98, -55.9) * mm, "mid": v(0, -59.87) * mm, "end": v(-3.98, -55.9) * mm});
            skLineSegment(sketch, "E506.1.left", {"start": v(3.98, -42.96) * mm, "end": v(3.98, -55.9) * mm});
            skLineSegment(sketch, "E506.1.right", {"start": v(-3.98, -42.96) * mm, "end": v(-3.98, -55.9) * mm});
            skLineSegment(sketch, "E507", {"start": v(76.78, 150.69) * mm, "end": v(73.69, 140.46) * mm, "construction": true});
            skPoint(sketch, "E507.startSnap0", {"position": v(138.49, 150.69) * mm});
            skLineSegment(sketch, "E508", {"start": v(89.28, -152.75) * mm, "end": v(79.29, -145.04) * mm, "construction": true});
            skPoint(sketch, "E509", {"position": v(73.69, 140.46) * mm});
            skLineSegment(sketch, "E510.MirrorCS", {"start": v(-89.28, -152.75) * mm, "end": v(-79.29, -145.04) * mm, "construction": true});
            skLineSegment(sketch, "E511.MirrorCS", {"start": v(-76.78, 150.69) * mm, "end": v(-73.69, 140.46) * mm, "construction": true});
            skArc(sketch, "E512.0.startCap", {"start": v(91.7, -149.6) * mm, "mid": v(92.43, -155.18) * mm, "end": v(86.85, -155.9) * mm});
            skArc(sketch, "E512.0.endCap", {"start": v(76.86, -148.19) * mm, "mid": v(76.14, -142.61) * mm, "end": v(81.72, -141.9) * mm});
            skLineSegment(sketch, "E512.0.left", {"start": v(86.85, -155.9) * mm, "end": v(76.86, -148.19) * mm});
            skLineSegment(sketch, "E512.0.right", {"start": v(91.7, -149.6) * mm, "end": v(81.72, -141.9) * mm});
            skArc(sketch, "E512.1.startCap", {"start": v(-86.85, -155.9) * mm, "mid": v(-92.43, -155.18) * mm, "end": v(-91.7, -149.6) * mm});
            skArc(sketch, "E512.1.endCap", {"start": v(-81.72, -141.9) * mm, "mid": v(-76.14, -142.61) * mm, "end": v(-76.86, -148.19) * mm});
            skLineSegment(sketch, "E512.1.left", {"start": v(-91.7, -149.6) * mm, "end": v(-81.72, -141.9) * mm});
            skLineSegment(sketch, "E512.1.right", {"start": v(-86.85, -155.9) * mm, "end": v(-76.86, -148.19) * mm});
            skArc(sketch, "E512.2.startCap", {"start": v(72.98, 151.84) * mm, "mid": v(77.93, 154.5) * mm, "end": v(80.59, 149.54) * mm});
            skArc(sketch, "E512.2.endCap", {"start": v(77.5, 139.31) * mm, "mid": v(72.54, 136.66) * mm, "end": v(69.88, 141.61) * mm});
            skLineSegment(sketch, "E512.2.left", {"start": v(80.59, 149.54) * mm, "end": v(77.5, 139.31) * mm});
            skLineSegment(sketch, "E512.2.right", {"start": v(72.98, 151.84) * mm, "end": v(69.88, 141.61) * mm});
            skArc(sketch, "E512.3.startCap", {"start": v(-80.59, 149.54) * mm, "mid": v(-77.93, 154.5) * mm, "end": v(-72.98, 151.84) * mm});
            skArc(sketch, "E512.3.endCap", {"start": v(-69.88, 141.61) * mm, "mid": v(-72.54, 136.66) * mm, "end": v(-77.5, 139.31) * mm});
            skLineSegment(sketch, "E512.3.left", {"start": v(-72.98, 151.84) * mm, "end": v(-69.88, 141.61) * mm});
            skLineSegment(sketch, "E512.3.right", {"start": v(-80.59, 149.54) * mm, "end": v(-77.5, 139.31) * mm});
            skSolve(sketch);
        }
        {
            var Q0;
            Q0 = qSketchRegion(id + "F2", true);
            extrude(context, id + "F3", {"entities" : qUnion([Q0]), "operationType" : NewBodyOperationType.ADD, "oppositeDirection" : true, "depth" : 3.17 * mm});
        }
    });
